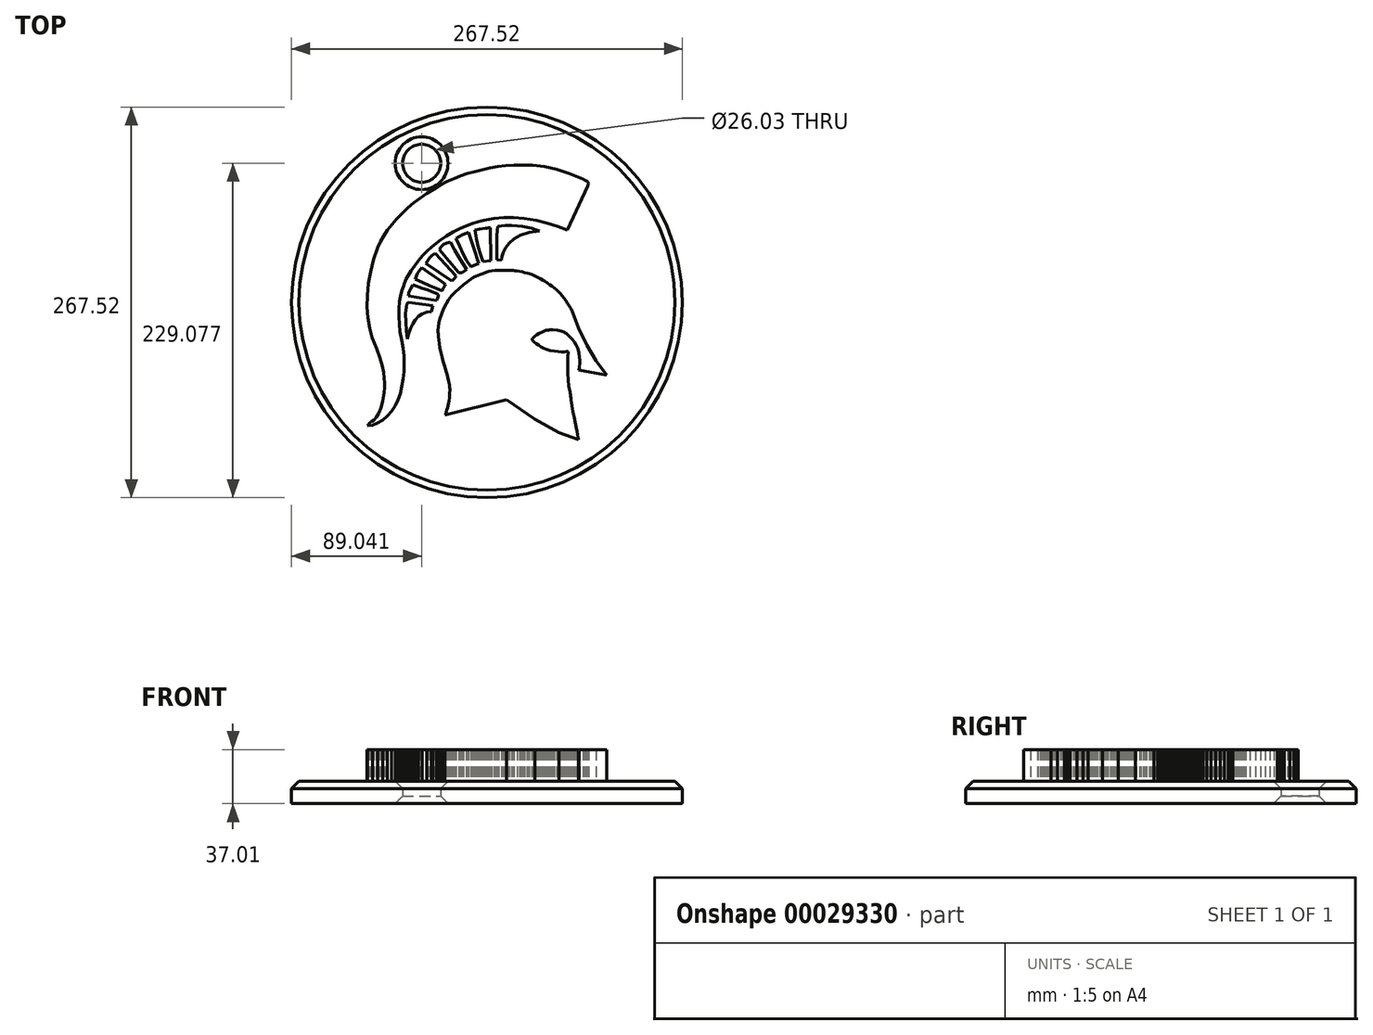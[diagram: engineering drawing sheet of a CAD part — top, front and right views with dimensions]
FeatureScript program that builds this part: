
annotation { "Feature Type Name" : "Feature", "Feature Type Description" : "" }
export const myFeature = defineFeature(function(context is Context, id is Id, definition is map)
    precondition{}
    {
        {
            var Q0;
            Q0=qCreatedBy(makeId("Top.planeOp"),FACE);
            var sketch = newSketch(context, id + "F0", { "sketchPlane" : qUnion([Q0])});
            skLineSegment(sketch, "E0", {"start": v(-81.82, -84.47) * mm, "end": v(-80.11, -82.47) * mm});
            skLineSegment(sketch, "E1", {"start": v(-80.11, -82.47) * mm, "end": v(-79.76, -82.32) * mm});
            skLineSegment(sketch, "E2", {"start": v(-79.76, -82.32) * mm, "end": v(-78.83, -81.76) * mm});
            skLineSegment(sketch, "E3", {"start": v(-78.83, -81.76) * mm, "end": v(-77.48, -80.64) * mm});
            skLineSegment(sketch, "E4", {"start": v(-77.48, -80.64) * mm, "end": v(-75.88, -78.83) * mm});
            skLineSegment(sketch, "E5", {"start": v(-75.88, -78.83) * mm, "end": v(-74.2, -76.16) * mm});
            skLineSegment(sketch, "E6", {"start": v(-74.2, -76.16) * mm, "end": v(-72.61, -72.5) * mm});
            skLineSegment(sketch, "E7", {"start": v(-72.61, -72.5) * mm, "end": v(-71.28, -67.7) * mm});
            skLineSegment(sketch, "E8", {"start": v(-71.28, -67.7) * mm, "end": v(-70.36, -61.6) * mm});
            skLineSegment(sketch, "E9", {"start": v(-70.36, -61.6) * mm, "end": v(-70.11, -58.43) * mm});
            skLineSegment(sketch, "E10", {"start": v(-70.11, -58.43) * mm, "end": v(-70.03, -55.21) * mm});
            skLineSegment(sketch, "E11", {"start": v(-70.03, -55.21) * mm, "end": v(-70.22, -51.75) * mm});
            skLineSegment(sketch, "E12", {"start": v(-70.22, -51.75) * mm, "end": v(-70.77, -47.86) * mm});
            skLineSegment(sketch, "E13", {"start": v(-70.77, -47.86) * mm, "end": v(-71.78, -43.35) * mm});
            skLineSegment(sketch, "E14", {"start": v(-71.78, -43.35) * mm, "end": v(-73.35, -38.02) * mm});
            skLineSegment(sketch, "E15", {"start": v(-73.35, -38.02) * mm, "end": v(-75.57, -31.7) * mm});
            skLineSegment(sketch, "E16", {"start": v(-75.57, -31.7) * mm, "end": v(-78.54, -24.17) * mm});
            skLineSegment(sketch, "E17", {"start": v(-78.54, -24.17) * mm, "end": v(-80.35, -17.68) * mm});
            skLineSegment(sketch, "E18", {"start": v(-80.35, -17.68) * mm, "end": v(-81.52, -10.62) * mm});
            skLineSegment(sketch, "E19", {"start": v(-81.52, -10.62) * mm, "end": v(-82.04, -3.1) * mm});
            skLineSegment(sketch, "E20", {"start": v(-82.04, -3.1) * mm, "end": v(-81.9, 4.77) * mm});
            skLineSegment(sketch, "E21", {"start": v(-81.9, 4.77) * mm, "end": v(-81.12, 12.88) * mm});
            skLineSegment(sketch, "E22", {"start": v(-81.12, 12.88) * mm, "end": v(-79.67, 21.1) * mm});
            skLineSegment(sketch, "E23", {"start": v(-79.67, 21.1) * mm, "end": v(-77.55, 29.32) * mm});
            skLineSegment(sketch, "E24", {"start": v(-77.55, 29.32) * mm, "end": v(-74.76, 37.44) * mm});
            skLineSegment(sketch, "E25", {"start": v(-74.76, 37.44) * mm, "end": v(-72.96, 41.45) * mm});
            skLineSegment(sketch, "E26", {"start": v(-72.96, 41.45) * mm, "end": v(-70.71, 45.46) * mm});
            skLineSegment(sketch, "E27", {"start": v(-70.71, 45.46) * mm, "end": v(-68.05, 49.45) * mm});
            skLineSegment(sketch, "E28", {"start": v(-68.05, 49.45) * mm, "end": v(-65.02, 53.39) * mm});
            skLineSegment(sketch, "E29", {"start": v(-65.02, 53.39) * mm, "end": v(-61.65, 57.26) * mm});
            skLineSegment(sketch, "E30", {"start": v(-61.65, 57.26) * mm, "end": v(-57.99, 61.03) * mm});
            skLineSegment(sketch, "E31", {"start": v(-57.99, 61.03) * mm, "end": v(-54.06, 64.68) * mm});
            skLineSegment(sketch, "E32", {"start": v(-54.06, 64.68) * mm, "end": v(-49.92, 68.19) * mm});
            skLineSegment(sketch, "E33", {"start": v(-49.92, 68.19) * mm, "end": v(-45.6, 71.53) * mm});
            skLineSegment(sketch, "E34", {"start": v(-45.6, 71.53) * mm, "end": v(-41.12, 74.68) * mm});
            skLineSegment(sketch, "E35", {"start": v(-41.12, 74.68) * mm, "end": v(-36.55, 77.6) * mm});
            skLineSegment(sketch, "E36", {"start": v(-36.55, 77.6) * mm, "end": v(-31.9, 80.3) * mm});
            skLineSegment(sketch, "E37", {"start": v(-31.9, 80.3) * mm, "end": v(-27.23, 82.72) * mm});
            skLineSegment(sketch, "E38", {"start": v(-27.23, 82.72) * mm, "end": v(-22.57, 84.86) * mm});
            skLineSegment(sketch, "E39", {"start": v(-22.57, 84.86) * mm, "end": v(-17.96, 86.68) * mm});
            skLineSegment(sketch, "E40", {"start": v(-17.96, 86.68) * mm, "end": v(-13.43, 88.16) * mm});
            skLineSegment(sketch, "E41", {"start": v(-13.43, 88.16) * mm, "end": v(-8.18, 89.63) * mm});
            skLineSegment(sketch, "E42", {"start": v(-8.18, 89.63) * mm, "end": v(-3.03, 90.91) * mm});
            skLineSegment(sketch, "E43", {"start": v(-3.03, 90.91) * mm, "end": v(2.11, 92) * mm});
            skLineSegment(sketch, "E44", {"start": v(2.11, 92) * mm, "end": v(7.35, 92.87) * mm});
            skLineSegment(sketch, "E45", {"start": v(7.35, 92.87) * mm, "end": v(12.8, 93.51) * mm});
            skLineSegment(sketch, "E46", {"start": v(12.8, 93.51) * mm, "end": v(18.53, 93.92) * mm});
            skLineSegment(sketch, "E47", {"start": v(18.53, 93.92) * mm, "end": v(24.67, 94.08) * mm});
            skLineSegment(sketch, "E48", {"start": v(24.67, 94.08) * mm, "end": v(31.31, 93.97) * mm});
            skLineSegment(sketch, "E49", {"start": v(31.31, 93.97) * mm, "end": v(39.54, 93.1) * mm});
            skLineSegment(sketch, "E50", {"start": v(39.54, 93.1) * mm, "end": v(47.72, 91.15) * mm});
            skLineSegment(sketch, "E51", {"start": v(47.72, 91.15) * mm, "end": v(56.34, 88.2) * mm});
            skLineSegment(sketch, "E52", {"start": v(56.34, 88.2) * mm, "end": v(65.9, 84.32) * mm});
            skLineSegment(sketch, "E53", {"start": v(65.9, 84.32) * mm, "end": v(66.02, 84.26) * mm});
            skLineSegment(sketch, "E54", {"start": v(66.02, 84.26) * mm, "end": v(66.35, 84.09) * mm});
            skLineSegment(sketch, "E55", {"start": v(66.35, 84.09) * mm, "end": v(66.82, 83.84) * mm});
            skLineSegment(sketch, "E56", {"start": v(66.82, 83.84) * mm, "end": v(67.38, 83.52) * mm});
            skLineSegment(sketch, "E57", {"start": v(67.38, 83.52) * mm, "end": v(67.97, 83.16) * mm});
            skLineSegment(sketch, "E58", {"start": v(67.97, 83.16) * mm, "end": v(68.54, 82.77) * mm});
            skLineSegment(sketch, "E59", {"start": v(68.54, 82.77) * mm, "end": v(69.01, 82.39) * mm});
            skLineSegment(sketch, "E60", {"start": v(69.01, 82.39) * mm, "end": v(69.34, 82.02) * mm});
            skLineSegment(sketch, "E61", {"start": v(69.34, 82.02) * mm, "end": v(69.55, 81.28) * mm});
            skLineSegment(sketch, "E62", {"start": v(69.55, 81.28) * mm, "end": v(69.37, 80.54) * mm});
            skLineSegment(sketch, "E63", {"start": v(69.37, 80.54) * mm, "end": v(69.07, 79.97) * mm});
            skLineSegment(sketch, "E64", {"start": v(69.07, 79.97) * mm, "end": v(68.92, 79.74) * mm});
            skLineSegment(sketch, "E65", {"start": v(68.92, 79.74) * mm, "end": v(55.1, 49.38) * mm});
            skLineSegment(sketch, "E66", {"start": v(55.1, 49.38) * mm, "end": v(48.24, 52.04) * mm});
            skLineSegment(sketch, "E67", {"start": v(48.24, 52.04) * mm, "end": v(41.22, 54.4) * mm});
            skLineSegment(sketch, "E68", {"start": v(41.22, 54.4) * mm, "end": v(33.72, 56.27) * mm});
            skLineSegment(sketch, "E69", {"start": v(33.72, 56.27) * mm, "end": v(25.43, 57.47) * mm});
            skLineSegment(sketch, "E70", {"start": v(25.43, 57.47) * mm, "end": v(18.16, 57.96) * mm});
            skLineSegment(sketch, "E71", {"start": v(18.16, 57.96) * mm, "end": v(11.43, 57.98) * mm});
            skLineSegment(sketch, "E72", {"start": v(11.43, 57.98) * mm, "end": v(4.83, 57.42) * mm});
            skLineSegment(sketch, "E73", {"start": v(4.83, 57.42) * mm, "end": v(-2.08, 56.17) * mm});
            skLineSegment(sketch, "E74", {"start": v(-2.08, 56.17) * mm, "end": v(-5.93, 55.2) * mm});
            skLineSegment(sketch, "E75", {"start": v(-5.93, 55.2) * mm, "end": v(-9.96, 53.98) * mm});
            skLineSegment(sketch, "E76", {"start": v(-9.96, 53.98) * mm, "end": v(-14.18, 52.43) * mm});
            skLineSegment(sketch, "E77", {"start": v(-14.18, 52.43) * mm, "end": v(-18.58, 50.5) * mm});
            skLineSegment(sketch, "E78", {"start": v(-18.58, 50.5) * mm, "end": v(-23.16, 48.14) * mm});
            skLineSegment(sketch, "E79", {"start": v(-23.16, 48.14) * mm, "end": v(-27.92, 45.3) * mm});
            skLineSegment(sketch, "E80", {"start": v(-27.92, 45.3) * mm, "end": v(-32.85, 41.88) * mm});
            skLineSegment(sketch, "E81", {"start": v(-32.85, 41.88) * mm, "end": v(-37.97, 37.87) * mm});
            skLineSegment(sketch, "E82", {"start": v(-37.97, 37.87) * mm, "end": v(-40.92, 35.16) * mm});
            skLineSegment(sketch, "E83", {"start": v(-40.92, 35.16) * mm, "end": v(-43.9, 32) * mm});
            skLineSegment(sketch, "E84", {"start": v(-43.9, 32) * mm, "end": v(-46.82, 28.56) * mm});
            skLineSegment(sketch, "E85", {"start": v(-46.82, 28.56) * mm, "end": v(-49.52, 25.05) * mm});
            skLineSegment(sketch, "E86", {"start": v(-49.52, 25.05) * mm, "end": v(-51.92, 21.65) * mm});
            skLineSegment(sketch, "E87", {"start": v(-51.92, 21.65) * mm, "end": v(-53.9, 18.55) * mm});
            skLineSegment(sketch, "E88", {"start": v(-53.9, 18.55) * mm, "end": v(-55.32, 15.94) * mm});
            skLineSegment(sketch, "E89", {"start": v(-55.32, 15.94) * mm, "end": v(-56.1, 14) * mm});
            skLineSegment(sketch, "E90", {"start": v(-56.1, 14) * mm, "end": v(-56.4, 13.21) * mm});
            skLineSegment(sketch, "E91", {"start": v(-56.4, 13.21) * mm, "end": v(-57.17, 11.04) * mm});
            skLineSegment(sketch, "E92", {"start": v(-57.17, 11.04) * mm, "end": v(-58.17, 7.82) * mm});
            skLineSegment(sketch, "E93", {"start": v(-58.17, 7.82) * mm, "end": v(-59.22, 3.9) * mm});
            skLineSegment(sketch, "E94", {"start": v(-59.22, 3.9) * mm, "end": v(-59.9, 0.65) * mm});
            skLineSegment(sketch, "E95", {"start": v(-59.9, 0.65) * mm, "end": v(-60.33, -4.33) * mm});
            skLineSegment(sketch, "E96", {"start": v(-60.33, -4.33) * mm, "end": v(-60.2, -9.72) * mm});
            skLineSegment(sketch, "E97", {"start": v(-60.2, -9.72) * mm, "end": v(-59.8, -15.07) * mm});
            skLineSegment(sketch, "E98", {"start": v(-59.8, -15.07) * mm, "end": v(-59.47, -19.88) * mm});
            skLineSegment(sketch, "E99", {"start": v(-59.47, -19.88) * mm, "end": v(-58.37, -26.08) * mm});
            skLineSegment(sketch, "E100", {"start": v(-58.37, -26.08) * mm, "end": v(-57.47, -31.55) * mm});
            skLineSegment(sketch, "E101", {"start": v(-57.47, -31.55) * mm, "end": v(-56.84, -36.7) * mm});
            skLineSegment(sketch, "E102", {"start": v(-56.84, -36.7) * mm, "end": v(-56.58, -41.88) * mm});
            skLineSegment(sketch, "E103", {"start": v(-56.58, -41.88) * mm, "end": v(-56.78, -47.2) * mm});
            skLineSegment(sketch, "E104", {"start": v(-56.78, -47.2) * mm, "end": v(-57.38, -52.46) * mm});
            skLineSegment(sketch, "E105", {"start": v(-57.38, -52.46) * mm, "end": v(-58.28, -57.61) * mm});
            skLineSegment(sketch, "E106", {"start": v(-58.28, -57.61) * mm, "end": v(-59.36, -62.55) * mm});
            skLineSegment(sketch, "E107", {"start": v(-59.36, -62.55) * mm, "end": v(-60.7, -66.75) * mm});
            skLineSegment(sketch, "E108", {"start": v(-60.7, -66.75) * mm, "end": v(-62.66, -70.77) * mm});
            skLineSegment(sketch, "E109", {"start": v(-62.66, -70.77) * mm, "end": v(-65.13, -74.48) * mm});
            skLineSegment(sketch, "E110", {"start": v(-65.13, -74.48) * mm, "end": v(-68.03, -77.78) * mm});
            skLineSegment(sketch, "E111", {"start": v(-68.03, -77.78) * mm, "end": v(-71.24, -80.55) * mm});
            skLineSegment(sketch, "E112", {"start": v(-71.24, -80.55) * mm, "end": v(-74.68, -82.66) * mm});
            skLineSegment(sketch, "E113", {"start": v(-74.68, -82.66) * mm, "end": v(-78.24, -84) * mm});
            skLineSegment(sketch, "E114", {"start": v(-78.24, -84) * mm, "end": v(-81.82, -84.47) * mm});
            skLineSegment(sketch, "E115", {"start": v(-54.53, -25.24) * mm, "end": v(-55.07, -19.51) * mm});
            skLineSegment(sketch, "E116", {"start": v(-55.07, -19.51) * mm, "end": v(-55.59, -13.77) * mm});
            skLineSegment(sketch, "E117", {"start": v(-55.59, -13.77) * mm, "end": v(-55.65, -7.67) * mm});
            skLineSegment(sketch, "E118", {"start": v(-55.65, -7.67) * mm, "end": v(-54.81, -0.87) * mm});
            skLineSegment(sketch, "E119", {"start": v(-54.81, -0.87) * mm, "end": v(-53.88, 0.13) * mm});
            skLineSegment(sketch, "E120", {"start": v(-53.88, 0.13) * mm, "end": v(-37.13, -2.22) * mm});
            skLineSegment(sketch, "E121", {"start": v(-37.13, -2.22) * mm, "end": v(-37.85, -6.21) * mm});
            skLineSegment(sketch, "E122", {"start": v(-37.85, -6.21) * mm, "end": v(-41.3, -6.74) * mm});
            skLineSegment(sketch, "E123", {"start": v(-41.3, -6.74) * mm, "end": v(-44.26, -7.92) * mm});
            skLineSegment(sketch, "E124", {"start": v(-44.26, -7.92) * mm, "end": v(-46.8, -9.68) * mm});
            skLineSegment(sketch, "E125", {"start": v(-46.8, -9.68) * mm, "end": v(-48.95, -11.97) * mm});
            skLineSegment(sketch, "E126", {"start": v(-48.95, -11.97) * mm, "end": v(-50.75, -14.73) * mm});
            skLineSegment(sketch, "E127", {"start": v(-50.75, -14.73) * mm, "end": v(-52.26, -17.9) * mm});
            skLineSegment(sketch, "E128", {"start": v(-52.26, -17.9) * mm, "end": v(-53.5, -21.42) * mm});
            skLineSegment(sketch, "E129", {"start": v(-53.5, -21.42) * mm, "end": v(-54.53, -25.24) * mm});
            skLineSegment(sketch, "E130", {"start": v(-28.63, -77.13) * mm, "end": v(-28.54, -76.85) * mm});
            skLineSegment(sketch, "E131", {"start": v(-28.54, -76.85) * mm, "end": v(-28.29, -76.07) * mm});
            skLineSegment(sketch, "E132", {"start": v(-28.29, -76.07) * mm, "end": v(-27.92, -74.93) * mm});
            skLineSegment(sketch, "E133", {"start": v(-27.92, -74.93) * mm, "end": v(-27.48, -73.52) * mm});
            skLineSegment(sketch, "E134", {"start": v(-27.48, -73.52) * mm, "end": v(-27.02, -71.97) * mm});
            skLineSegment(sketch, "E135", {"start": v(-27.02, -71.97) * mm, "end": v(-26.57, -70.4) * mm});
            skLineSegment(sketch, "E136", {"start": v(-26.57, -70.4) * mm, "end": v(-26.18, -68.9) * mm});
            skLineSegment(sketch, "E137", {"start": v(-26.18, -68.9) * mm, "end": v(-25.9, -67.6) * mm});
            skLineSegment(sketch, "E138", {"start": v(-25.9, -67.6) * mm, "end": v(-25.58, -64.97) * mm});
            skLineSegment(sketch, "E139", {"start": v(-25.58, -64.97) * mm, "end": v(-25.44, -62.18) * mm});
            skLineSegment(sketch, "E140", {"start": v(-25.44, -62.18) * mm, "end": v(-25.4, -59.98) * mm});
            skLineSegment(sketch, "E141", {"start": v(-25.4, -59.98) * mm, "end": v(-25.4, -59.09) * mm});
            skLineSegment(sketch, "E142", {"start": v(-25.4, -59.09) * mm, "end": v(-25.5, -58.38) * mm});
            skLineSegment(sketch, "E143", {"start": v(-25.5, -58.38) * mm, "end": v(-25.75, -56.56) * mm});
            skLineSegment(sketch, "E144", {"start": v(-25.75, -56.56) * mm, "end": v(-26.19, -54.03) * mm});
            skLineSegment(sketch, "E145", {"start": v(-26.19, -54.03) * mm, "end": v(-26.82, -51.22) * mm});
            skLineSegment(sketch, "E146", {"start": v(-26.82, -51.22) * mm, "end": v(-27.25, -49.6) * mm});
            skLineSegment(sketch, "E147", {"start": v(-27.25, -49.6) * mm, "end": v(-27.8, -47.67) * mm});
            skLineSegment(sketch, "E148", {"start": v(-27.8, -47.67) * mm, "end": v(-28.42, -45.53) * mm});
            skLineSegment(sketch, "E149", {"start": v(-28.42, -45.53) * mm, "end": v(-29.06, -43.3) * mm});
            skLineSegment(sketch, "E150", {"start": v(-29.06, -43.3) * mm, "end": v(-29.69, -41.13) * mm});
            skLineSegment(sketch, "E151", {"start": v(-29.69, -41.13) * mm, "end": v(-30.25, -39.11) * mm});
            skLineSegment(sketch, "E152", {"start": v(-30.25, -39.11) * mm, "end": v(-30.71, -37.4) * mm});
            skLineSegment(sketch, "E153", {"start": v(-30.71, -37.4) * mm, "end": v(-31.02, -36.08) * mm});
            skLineSegment(sketch, "E154", {"start": v(-31.02, -36.08) * mm, "end": v(-31.67, -33.63) * mm});
            skLineSegment(sketch, "E155", {"start": v(-31.67, -33.63) * mm, "end": v(-32.2, -30.97) * mm});
            skLineSegment(sketch, "E156", {"start": v(-32.2, -30.97) * mm, "end": v(-32.63, -28.27) * mm});
            skLineSegment(sketch, "E157", {"start": v(-32.63, -28.27) * mm, "end": v(-32.95, -25.69) * mm});
            skLineSegment(sketch, "E158", {"start": v(-32.95, -25.69) * mm, "end": v(-33.2, -23.4) * mm});
            skLineSegment(sketch, "E159", {"start": v(-33.2, -23.4) * mm, "end": v(-33.35, -21.55) * mm});
            skLineSegment(sketch, "E160", {"start": v(-33.35, -21.55) * mm, "end": v(-33.44, -20.32) * mm});
            skLineSegment(sketch, "E161", {"start": v(-33.44, -20.32) * mm, "end": v(-33.47, -19.88) * mm});
            skLineSegment(sketch, "E162", {"start": v(-33.47, -19.88) * mm, "end": v(-33.4, -18.95) * mm});
            skLineSegment(sketch, "E163", {"start": v(-33.4, -18.95) * mm, "end": v(-33.16, -16.7) * mm});
            skLineSegment(sketch, "E164", {"start": v(-33.16, -16.7) * mm, "end": v(-32.78, -13.95) * mm});
            skLineSegment(sketch, "E165", {"start": v(-32.78, -13.95) * mm, "end": v(-32.25, -11.5) * mm});
            skLineSegment(sketch, "E166", {"start": v(-32.25, -11.5) * mm, "end": v(-31.06, -7.95) * mm});
            skLineSegment(sketch, "E167", {"start": v(-31.06, -7.95) * mm, "end": v(-29.6, -4.42) * mm});
            skLineSegment(sketch, "E168", {"start": v(-29.6, -4.42) * mm, "end": v(-27.95, -1.1) * mm});
            skLineSegment(sketch, "E169", {"start": v(-27.95, -1.1) * mm, "end": v(-26.22, 1.82) * mm});
            skLineSegment(sketch, "E170", {"start": v(-26.22, 1.82) * mm, "end": v(-24.28, 4.32) * mm});
            skLineSegment(sketch, "E171", {"start": v(-24.28, 4.32) * mm, "end": v(-21.77, 6.93) * mm});
            skLineSegment(sketch, "E172", {"start": v(-21.77, 6.93) * mm, "end": v(-18.95, 9.51) * mm});
            skLineSegment(sketch, "E173", {"start": v(-18.95, 9.51) * mm, "end": v(-16.07, 11.92) * mm});
            skLineSegment(sketch, "E174", {"start": v(-16.07, 11.92) * mm, "end": v(-13.4, 14.04) * mm});
            skLineSegment(sketch, "E175", {"start": v(-13.4, 14.04) * mm, "end": v(-11.17, 15.71) * mm});
            skLineSegment(sketch, "E176", {"start": v(-11.17, 15.71) * mm, "end": v(-9.64, 16.82) * mm});
            skLineSegment(sketch, "E177", {"start": v(-9.64, 16.82) * mm, "end": v(-9.08, 17.21) * mm});
            skLineSegment(sketch, "E178", {"start": v(-9.08, 17.21) * mm, "end": v(-8.73, 17.37) * mm});
            skLineSegment(sketch, "E179", {"start": v(-8.73, 17.37) * mm, "end": v(-7.79, 17.78) * mm});
            skLineSegment(sketch, "E180", {"start": v(-7.79, 17.78) * mm, "end": v(-6.36, 18.37) * mm});
            skLineSegment(sketch, "E181", {"start": v(-6.36, 18.37) * mm, "end": v(-4.6, 19.08) * mm});
            skLineSegment(sketch, "E182", {"start": v(-4.6, 19.08) * mm, "end": v(-2.63, 19.82) * mm});
            skLineSegment(sketch, "E183", {"start": v(-2.63, 19.82) * mm, "end": v(-0.57, 20.54) * mm});
            skLineSegment(sketch, "E184", {"start": v(-0.57, 20.54) * mm, "end": v(1.43, 21.14) * mm});
            skLineSegment(sketch, "E185", {"start": v(1.43, 21.14) * mm, "end": v(3.26, 21.57) * mm});
            skLineSegment(sketch, "E186", {"start": v(3.26, 21.57) * mm, "end": v(5.53, 21.8) * mm});
            skLineSegment(sketch, "E187", {"start": v(5.53, 21.8) * mm, "end": v(7.95, 21.93) * mm});
            skLineSegment(sketch, "E188", {"start": v(7.95, 21.93) * mm, "end": v(10.39, 22) * mm});
            skLineSegment(sketch, "E189", {"start": v(10.39, 22) * mm, "end": v(12.7, 22.02) * mm});
            skLineSegment(sketch, "E190", {"start": v(12.7, 22.02) * mm, "end": v(14.74, 22) * mm});
            skLineSegment(sketch, "E191", {"start": v(14.74, 22) * mm, "end": v(16.37, 21.98) * mm});
            skLineSegment(sketch, "E192", {"start": v(16.37, 21.98) * mm, "end": v(17.45, 21.96) * mm});
            skLineSegment(sketch, "E193", {"start": v(17.45, 21.96) * mm, "end": v(17.84, 21.95) * mm});
            skLineSegment(sketch, "E194", {"start": v(17.84, 21.95) * mm, "end": v(18.18, 21.9) * mm});
            skLineSegment(sketch, "E195", {"start": v(18.18, 21.9) * mm, "end": v(19.13, 21.74) * mm});
            skLineSegment(sketch, "E196", {"start": v(19.13, 21.74) * mm, "end": v(20.53, 21.5) * mm});
            skLineSegment(sketch, "E197", {"start": v(20.53, 21.5) * mm, "end": v(22.23, 21.19) * mm});
            skLineSegment(sketch, "E198", {"start": v(22.23, 21.19) * mm, "end": v(24.1, 20.82) * mm});
            skLineSegment(sketch, "E199", {"start": v(24.1, 20.82) * mm, "end": v(25.96, 20.43) * mm});
            skLineSegment(sketch, "E200", {"start": v(25.96, 20.43) * mm, "end": v(27.69, 20.01) * mm});
            skLineSegment(sketch, "E201", {"start": v(27.69, 20.01) * mm, "end": v(29.13, 19.6) * mm});
            skLineSegment(sketch, "E202", {"start": v(29.13, 19.6) * mm, "end": v(30.92, 18.92) * mm});
            skLineSegment(sketch, "E203", {"start": v(30.92, 18.92) * mm, "end": v(32.84, 18.06) * mm});
            skLineSegment(sketch, "E204", {"start": v(32.84, 18.06) * mm, "end": v(34.77, 17.1) * mm});
            skLineSegment(sketch, "E205", {"start": v(34.77, 17.1) * mm, "end": v(36.61, 16.13) * mm});
            skLineSegment(sketch, "E206", {"start": v(36.61, 16.13) * mm, "end": v(38.24, 15.23) * mm});
            skLineSegment(sketch, "E207", {"start": v(38.24, 15.23) * mm, "end": v(39.54, 14.48) * mm});
            skLineSegment(sketch, "E208", {"start": v(39.54, 14.48) * mm, "end": v(40.4, 13.97) * mm});
            skLineSegment(sketch, "E209", {"start": v(40.4, 13.97) * mm, "end": v(40.71, 13.79) * mm});
            skLineSegment(sketch, "E210", {"start": v(40.71, 13.79) * mm, "end": v(41.01, 13.57) * mm});
            skLineSegment(sketch, "E211", {"start": v(41.01, 13.57) * mm, "end": v(41.82, 12.99) * mm});
            skLineSegment(sketch, "E212", {"start": v(41.82, 12.99) * mm, "end": v(43, 12.1) * mm});
            skLineSegment(sketch, "E213", {"start": v(43, 12.1) * mm, "end": v(44.45, 11) * mm});
            skLineSegment(sketch, "E214", {"start": v(44.45, 11) * mm, "end": v(46.03, 9.75) * mm});
            skLineSegment(sketch, "E215", {"start": v(46.03, 9.75) * mm, "end": v(47.62, 8.44) * mm});
            skLineSegment(sketch, "E216", {"start": v(47.62, 8.44) * mm, "end": v(49.08, 7.15) * mm});
            skLineSegment(sketch, "E217", {"start": v(49.08, 7.15) * mm, "end": v(50.3, 5.94) * mm});
            skLineSegment(sketch, "E218", {"start": v(50.3, 5.94) * mm, "end": v(51.48, 4.57) * mm});
            skLineSegment(sketch, "E219", {"start": v(51.48, 4.57) * mm, "end": v(52.74, 2.92) * mm});
            skLineSegment(sketch, "E220", {"start": v(52.74, 2.92) * mm, "end": v(54, 1.15) * mm});
            skLineSegment(sketch, "E221", {"start": v(54, 1.15) * mm, "end": v(55.2, -0.6) * mm});
            skLineSegment(sketch, "E222", {"start": v(55.2, -0.6) * mm, "end": v(56.24, -2.21) * mm});
            skLineSegment(sketch, "E223", {"start": v(56.24, -2.21) * mm, "end": v(57.09, -3.54) * mm});
            skLineSegment(sketch, "E224", {"start": v(57.09, -3.54) * mm, "end": v(57.65, -4.43) * mm});
            skLineSegment(sketch, "E225", {"start": v(57.65, -4.43) * mm, "end": v(57.85, -4.76) * mm});
            skLineSegment(sketch, "E226", {"start": v(57.85, -4.76) * mm, "end": v(62.78, -17.36) * mm});
            skLineSegment(sketch, "E227", {"start": v(62.78, -17.36) * mm, "end": v(68.43, -29.1) * mm});
            skLineSegment(sketch, "E228", {"start": v(68.43, -29.1) * mm, "end": v(74.84, -39.93) * mm});
            skLineSegment(sketch, "E229", {"start": v(74.84, -39.93) * mm, "end": v(82.04, -49.81) * mm});
            skLineSegment(sketch, "E230", {"start": v(82.04, -49.81) * mm, "end": v(62.89, -46.29) * mm});
            skLineSegment(sketch, "E231", {"start": v(62.89, -46.29) * mm, "end": v(62.97, -45.98) * mm});
            skLineSegment(sketch, "E232", {"start": v(62.97, -45.98) * mm, "end": v(63.16, -45.1) * mm});
            skLineSegment(sketch, "E233", {"start": v(63.16, -45.1) * mm, "end": v(63.38, -43.74) * mm});
            skLineSegment(sketch, "E234", {"start": v(63.38, -43.74) * mm, "end": v(63.55, -41.94) * mm});
            skLineSegment(sketch, "E235", {"start": v(63.55, -41.94) * mm, "end": v(63.6, -39.79) * mm});
            skLineSegment(sketch, "E236", {"start": v(63.6, -39.79) * mm, "end": v(63.43, -37.34) * mm});
            skLineSegment(sketch, "E237", {"start": v(63.43, -37.34) * mm, "end": v(63, -34.68) * mm});
            skLineSegment(sketch, "E238", {"start": v(63, -34.68) * mm, "end": v(62.2, -31.86) * mm});
            skLineSegment(sketch, "E239", {"start": v(62.2, -31.86) * mm, "end": v(61.05, -29.23) * mm});
            skLineSegment(sketch, "E240", {"start": v(61.05, -29.23) * mm, "end": v(59.7, -26.95) * mm});
            skLineSegment(sketch, "E241", {"start": v(59.7, -26.95) * mm, "end": v(58.23, -25.03) * mm});
            skLineSegment(sketch, "E242", {"start": v(58.23, -25.03) * mm, "end": v(56.77, -23.46) * mm});
            skLineSegment(sketch, "E243", {"start": v(56.77, -23.46) * mm, "end": v(55.43, -22.24) * mm});
            skLineSegment(sketch, "E244", {"start": v(55.43, -22.24) * mm, "end": v(54.33, -21.38) * mm});
            skLineSegment(sketch, "E245", {"start": v(54.33, -21.38) * mm, "end": v(53.59, -20.86) * mm});
            skLineSegment(sketch, "E246", {"start": v(53.59, -20.86) * mm, "end": v(53.31, -20.69) * mm});
            skLineSegment(sketch, "E247", {"start": v(53.31, -20.69) * mm, "end": v(52.71, -20.39) * mm});
            skLineSegment(sketch, "E248", {"start": v(52.71, -20.39) * mm, "end": v(51.03, -19.73) * mm});
            skLineSegment(sketch, "E249", {"start": v(51.03, -19.73) * mm, "end": v(48.48, -19.05) * mm});
            skLineSegment(sketch, "E250", {"start": v(48.48, -19.05) * mm, "end": v(45.26, -18.71) * mm});
            skLineSegment(sketch, "E251", {"start": v(45.26, -18.71) * mm, "end": v(44.61, -18.72) * mm});
            skLineSegment(sketch, "E252", {"start": v(44.61, -18.72) * mm, "end": v(43.86, -18.77) * mm});
            skLineSegment(sketch, "E253", {"start": v(43.86, -18.77) * mm, "end": v(43.05, -18.83) * mm});
            skLineSegment(sketch, "E254", {"start": v(43.05, -18.83) * mm, "end": v(42.25, -18.91) * mm});
            skLineSegment(sketch, "E255", {"start": v(42.25, -18.91) * mm, "end": v(41.52, -18.99) * mm});
            skLineSegment(sketch, "E256", {"start": v(41.52, -18.99) * mm, "end": v(40.92, -19.06) * mm});
            skLineSegment(sketch, "E257", {"start": v(40.92, -19.06) * mm, "end": v(40.51, -19.1) * mm});
            skLineSegment(sketch, "E258", {"start": v(40.51, -19.1) * mm, "end": v(40.37, -19.13) * mm});
            skLineSegment(sketch, "E259", {"start": v(40.37, -19.13) * mm, "end": v(37.89, -20.17) * mm});
            skLineSegment(sketch, "E260", {"start": v(37.89, -20.17) * mm, "end": v(35.84, -21.26) * mm});
            skLineSegment(sketch, "E261", {"start": v(35.84, -21.26) * mm, "end": v(34.18, -22.33) * mm});
            skLineSegment(sketch, "E262", {"start": v(34.18, -22.33) * mm, "end": v(32.9, -23.33) * mm});
            skLineSegment(sketch, "E263", {"start": v(32.9, -23.33) * mm, "end": v(31.94, -24.2) * mm});
            skLineSegment(sketch, "E264", {"start": v(31.94, -24.2) * mm, "end": v(31.3, -24.9) * mm});
            skLineSegment(sketch, "E265", {"start": v(31.3, -24.9) * mm, "end": v(30.94, -25.36) * mm});
            skLineSegment(sketch, "E266", {"start": v(30.94, -25.36) * mm, "end": v(30.82, -25.52) * mm});
            skLineSegment(sketch, "E267", {"start": v(30.82, -25.52) * mm, "end": v(31.05, -25.74) * mm});
            skLineSegment(sketch, "E268", {"start": v(31.05, -25.74) * mm, "end": v(31.67, -26.32) * mm});
            skLineSegment(sketch, "E269", {"start": v(31.67, -26.32) * mm, "end": v(32.64, -27.17) * mm});
            skLineSegment(sketch, "E270", {"start": v(32.64, -27.17) * mm, "end": v(33.9, -28.2) * mm});
            skLineSegment(sketch, "E271", {"start": v(33.9, -28.2) * mm, "end": v(35.38, -29.3) * mm});
            skLineSegment(sketch, "E272", {"start": v(35.38, -29.3) * mm, "end": v(37.03, -30.37) * mm});
            skLineSegment(sketch, "E273", {"start": v(37.03, -30.37) * mm, "end": v(38.79, -31.33) * mm});
            skLineSegment(sketch, "E274", {"start": v(38.79, -31.33) * mm, "end": v(40.6, -32.08) * mm});
            skLineSegment(sketch, "E275", {"start": v(40.6, -32.08) * mm, "end": v(43.43, -32.87) * mm});
            skLineSegment(sketch, "E276", {"start": v(43.43, -32.87) * mm, "end": v(46.16, -33.4) * mm});
            skLineSegment(sketch, "E277", {"start": v(46.16, -33.4) * mm, "end": v(48.7, -33.7) * mm});
            skLineSegment(sketch, "E278", {"start": v(48.7, -33.7) * mm, "end": v(50.97, -33.83) * mm});
            skLineSegment(sketch, "E279", {"start": v(50.97, -33.83) * mm, "end": v(52.88, -33.85) * mm});
            skLineSegment(sketch, "E280", {"start": v(52.88, -33.85) * mm, "end": v(54.35, -33.8) * mm});
            skLineSegment(sketch, "E281", {"start": v(54.35, -33.8) * mm, "end": v(55.3, -33.72) * mm});
            skLineSegment(sketch, "E282", {"start": v(55.3, -33.72) * mm, "end": v(55.63, -33.69) * mm});
            skLineSegment(sketch, "E283", {"start": v(55.63, -33.69) * mm, "end": v(55.59, -34.5) * mm});
            skLineSegment(sketch, "E284", {"start": v(55.59, -34.5) * mm, "end": v(55.48, -36.71) * mm});
            skLineSegment(sketch, "E285", {"start": v(55.48, -36.71) * mm, "end": v(55.38, -40.01) * mm});
            skLineSegment(sketch, "E286", {"start": v(55.38, -40.01) * mm, "end": v(55.34, -44.07) * mm});
            skLineSegment(sketch, "E287", {"start": v(55.34, -44.07) * mm, "end": v(55.41, -48.56) * mm});
            skLineSegment(sketch, "E288", {"start": v(55.41, -48.56) * mm, "end": v(55.65, -53.17) * mm});
            skLineSegment(sketch, "E289", {"start": v(55.65, -53.17) * mm, "end": v(56.13, -57.56) * mm});
            skLineSegment(sketch, "E290", {"start": v(56.13, -57.56) * mm, "end": v(56.89, -61.42) * mm});
            skLineSegment(sketch, "E291", {"start": v(56.89, -61.42) * mm, "end": v(57.04, -62.2) * mm});
            skLineSegment(sketch, "E292", {"start": v(57.04, -62.2) * mm, "end": v(57.14, -62.89) * mm});
            skLineSegment(sketch, "E293", {"start": v(57.14, -62.89) * mm, "end": v(57.32, -64.36) * mm});
            skLineSegment(sketch, "E294", {"start": v(57.32, -64.36) * mm, "end": v(57.42, -65.36) * mm});
            skLineSegment(sketch, "E295", {"start": v(57.42, -65.36) * mm, "end": v(57.48, -65.83) * mm});
            skLineSegment(sketch, "E296", {"start": v(57.48, -65.83) * mm, "end": v(57.53, -66.17) * mm});
            skLineSegment(sketch, "E297", {"start": v(57.53, -66.17) * mm, "end": v(57.6, -66.74) * mm});
            skLineSegment(sketch, "E298", {"start": v(57.6, -66.74) * mm, "end": v(58.17, -70.86) * mm});
            skLineSegment(sketch, "E299", {"start": v(58.17, -70.86) * mm, "end": v(58.97, -75.1) * mm});
            skLineSegment(sketch, "E300", {"start": v(58.97, -75.1) * mm, "end": v(59.76, -78.71) * mm});
            skLineSegment(sketch, "E301", {"start": v(59.76, -78.71) * mm, "end": v(60.48, -82.18) * mm});
            skLineSegment(sketch, "E302", {"start": v(60.48, -82.18) * mm, "end": v(61.12, -85.4) * mm});
            skLineSegment(sketch, "E303", {"start": v(61.12, -85.4) * mm, "end": v(61.68, -88.25) * mm});
            skLineSegment(sketch, "E304", {"start": v(61.68, -88.25) * mm, "end": v(62.13, -90.64) * mm});
            skLineSegment(sketch, "E305", {"start": v(62.13, -90.64) * mm, "end": v(62.47, -92.48) * mm});
            skLineSegment(sketch, "E306", {"start": v(62.47, -92.48) * mm, "end": v(62.68, -93.66) * mm});
            skLineSegment(sketch, "E307", {"start": v(62.68, -93.66) * mm, "end": v(62.76, -94.08) * mm});
            skLineSegment(sketch, "E308", {"start": v(62.76, -94.08) * mm, "end": v(49.18, -89.1) * mm});
            skLineSegment(sketch, "E309", {"start": v(49.18, -89.1) * mm, "end": v(32.97, -79.9) * mm});
            skLineSegment(sketch, "E310", {"start": v(32.97, -79.9) * mm, "end": v(13.4, -66.65) * mm});
            skLineSegment(sketch, "E311", {"start": v(13.4, -66.65) * mm, "end": v(-28.63, -77.13) * mm});
            skLineSegment(sketch, "E312", {"start": v(6.91, 29.14) * mm, "end": v(6.77, 34.65) * mm});
            skLineSegment(sketch, "E313", {"start": v(6.77, 34.65) * mm, "end": v(6.71, 40.24) * mm});
            skLineSegment(sketch, "E314", {"start": v(6.71, 40.24) * mm, "end": v(6.86, 46) * mm});
            skLineSegment(sketch, "E315", {"start": v(6.86, 46) * mm, "end": v(7.34, 52.02) * mm});
            skLineSegment(sketch, "E316", {"start": v(7.34, 52.02) * mm, "end": v(12.42, 52.54) * mm});
            skLineSegment(sketch, "E317", {"start": v(12.42, 52.54) * mm, "end": v(16.87, 52.7) * mm});
            skLineSegment(sketch, "E318", {"start": v(16.87, 52.7) * mm, "end": v(20.8, 52.53) * mm});
            skLineSegment(sketch, "E319", {"start": v(20.8, 52.53) * mm, "end": v(24.31, 52.1) * mm});
            skLineSegment(sketch, "E320", {"start": v(24.31, 52.1) * mm, "end": v(27.5, 51.48) * mm});
            skLineSegment(sketch, "E321", {"start": v(27.5, 51.48) * mm, "end": v(30.45, 50.72) * mm});
            skLineSegment(sketch, "E322", {"start": v(30.45, 50.72) * mm, "end": v(33.27, 49.88) * mm});
            skLineSegment(sketch, "E323", {"start": v(33.27, 49.88) * mm, "end": v(36.06, 49.02) * mm});
            skLineSegment(sketch, "E324", {"start": v(36.06, 49.02) * mm, "end": v(28.88, 47.98) * mm});
            skLineSegment(sketch, "E325", {"start": v(28.88, 47.98) * mm, "end": v(23.1, 46.07) * mm});
            skLineSegment(sketch, "E326", {"start": v(23.1, 46.07) * mm, "end": v(18.6, 43.53) * mm});
            skLineSegment(sketch, "E327", {"start": v(18.6, 43.53) * mm, "end": v(15.2, 40.57) * mm});
            skLineSegment(sketch, "E328", {"start": v(15.2, 40.57) * mm, "end": v(12.77, 37.42) * mm});
            skLineSegment(sketch, "E329", {"start": v(12.77, 37.42) * mm, "end": v(11.18, 34.3) * mm});
            skLineSegment(sketch, "E330", {"start": v(11.18, 34.3) * mm, "end": v(10.27, 31.41) * mm});
            skLineSegment(sketch, "E331", {"start": v(10.27, 31.41) * mm, "end": v(9.9, 29) * mm});
            skLineSegment(sketch, "E332", {"start": v(9.9, 29) * mm, "end": v(6.91, 29.14) * mm});
            skLineSegment(sketch, "E333", {"start": v(-8.2, 49.45) * mm, "end": v(-5.31, 50.04) * mm});
            skLineSegment(sketch, "E334", {"start": v(-5.31, 50.04) * mm, "end": v(-2.98, 50.46) * mm});
            skLineSegment(sketch, "E335", {"start": v(-2.98, 50.46) * mm, "end": v(-1.15, 50.75) * mm});
            skLineSegment(sketch, "E336", {"start": v(-1.15, 50.75) * mm, "end": v(0.22, 50.94) * mm});
            skLineSegment(sketch, "E337", {"start": v(0.22, 50.94) * mm, "end": v(1.2, 51.04) * mm});
            skLineSegment(sketch, "E338", {"start": v(1.2, 51.04) * mm, "end": v(1.83, 51.09) * mm});
            skLineSegment(sketch, "E339", {"start": v(1.83, 51.09) * mm, "end": v(2.18, 51.1) * mm});
            skLineSegment(sketch, "E340", {"start": v(2.18, 51.1) * mm, "end": v(2.28, 51.1) * mm});
            skLineSegment(sketch, "E341", {"start": v(2.28, 51.1) * mm, "end": v(2.78, 28.57) * mm});
            skLineSegment(sketch, "E342", {"start": v(2.78, 28.57) * mm, "end": v(-2.78, 27.79) * mm});
            skLineSegment(sketch, "E343", {"start": v(-2.78, 27.79) * mm, "end": v(-4.37, 32.7) * mm});
            skLineSegment(sketch, "E344", {"start": v(-4.37, 32.7) * mm, "end": v(-5.84, 37.85) * mm});
            skLineSegment(sketch, "E345", {"start": v(-5.84, 37.85) * mm, "end": v(-7.14, 43.38) * mm});
            skLineSegment(sketch, "E346", {"start": v(-7.14, 43.38) * mm, "end": v(-8.2, 49.45) * mm});
            skLineSegment(sketch, "E347", {"start": v(-12.47, 47.81) * mm, "end": v(-9.1, 37.44) * mm});
            skLineSegment(sketch, "E348", {"start": v(-9.1, 37.44) * mm, "end": v(-5.7, 26.57) * mm});
            skLineSegment(sketch, "E349", {"start": v(-5.7, 26.57) * mm, "end": v(-10.98, 24.44) * mm});
            skLineSegment(sketch, "E350", {"start": v(-10.98, 24.44) * mm, "end": v(-13.72, 28.65) * mm});
            skLineSegment(sketch, "E351", {"start": v(-13.72, 28.65) * mm, "end": v(-16.29, 33.35) * mm});
            skLineSegment(sketch, "E352", {"start": v(-16.29, 33.35) * mm, "end": v(-18.71, 38.44) * mm});
            skLineSegment(sketch, "E353", {"start": v(-18.71, 38.44) * mm, "end": v(-21.03, 43.82) * mm});
            skLineSegment(sketch, "E354", {"start": v(-21.03, 43.82) * mm, "end": v(-16.68, 46.24) * mm});
            skLineSegment(sketch, "E355", {"start": v(-16.68, 46.24) * mm, "end": v(-12.47, 47.81) * mm});
            skLineSegment(sketch, "E356", {"start": v(-25.02, 41.33) * mm, "end": v(-27.64, 40.71) * mm});
            skLineSegment(sketch, "E357", {"start": v(-27.64, 40.71) * mm, "end": v(-29.63, 39.53) * mm});
            skLineSegment(sketch, "E358", {"start": v(-29.63, 39.53) * mm, "end": v(-31.21, 37.96) * mm});
            skLineSegment(sketch, "E359", {"start": v(-31.21, 37.96) * mm, "end": v(-32.57, 36.2) * mm});
            skLineSegment(sketch, "E360", {"start": v(-32.57, 36.2) * mm, "end": v(-19.25, 20.3) * mm});
            skLineSegment(sketch, "E361", {"start": v(-19.25, 20.3) * mm, "end": v(-18.54, 20.2) * mm});
            skLineSegment(sketch, "E362", {"start": v(-18.54, 20.2) * mm, "end": v(-18.02, 20.17) * mm});
            skLineSegment(sketch, "E363", {"start": v(-18.02, 20.17) * mm, "end": v(-17.6, 20.16) * mm});
            skLineSegment(sketch, "E364", {"start": v(-17.6, 20.16) * mm, "end": v(-17.18, 20.16) * mm});
            skLineSegment(sketch, "E365", {"start": v(-17.18, 20.16) * mm, "end": v(-13.9, 22.51) * mm});
            skLineSegment(sketch, "E366", {"start": v(-13.9, 22.51) * mm, "end": v(-16.63, 26.88) * mm});
            skLineSegment(sketch, "E367", {"start": v(-16.63, 26.88) * mm, "end": v(-19.33, 31.16) * mm});
            skLineSegment(sketch, "E368", {"start": v(-19.33, 31.16) * mm, "end": v(-22.1, 35.82) * mm});
            skLineSegment(sketch, "E369", {"start": v(-22.1, 35.82) * mm, "end": v(-25.02, 41.33) * mm});
            skLineSegment(sketch, "E370", {"start": v(-41.7, 26.72) * mm, "end": v(-40.56, 28.53) * mm});
            skLineSegment(sketch, "E371", {"start": v(-40.56, 28.53) * mm, "end": v(-39.26, 30.31) * mm});
            skLineSegment(sketch, "E372", {"start": v(-39.26, 30.31) * mm, "end": v(-37.65, 32.03) * mm});
            skLineSegment(sketch, "E373", {"start": v(-37.65, 32.03) * mm, "end": v(-35.57, 33.63) * mm});
            skLineSegment(sketch, "E374", {"start": v(-35.57, 33.63) * mm, "end": v(-21.03, 18.02) * mm});
            skLineSegment(sketch, "E375", {"start": v(-21.03, 18.02) * mm, "end": v(-21.7, 16.85) * mm});
            skLineSegment(sketch, "E376", {"start": v(-21.7, 16.85) * mm, "end": v(-22.8, 15.81) * mm});
            skLineSegment(sketch, "E377", {"start": v(-22.8, 15.81) * mm, "end": v(-24.1, 14.53) * mm});
            skLineSegment(sketch, "E378", {"start": v(-24.1, 14.53) * mm, "end": v(-41.7, 26.72) * mm});
            skLineSegment(sketch, "E379", {"start": v(-44.76, 23.65) * mm, "end": v(-47.47, 20.02) * mm});
            skLineSegment(sketch, "E380", {"start": v(-47.47, 20.02) * mm, "end": v(-49.04, 15.95) * mm});
            skLineSegment(sketch, "E381", {"start": v(-49.04, 15.95) * mm, "end": v(-44.05, 13.7) * mm});
            skLineSegment(sketch, "E382", {"start": v(-44.05, 13.7) * mm, "end": v(-39.14, 11.5) * mm});
            skLineSegment(sketch, "E383", {"start": v(-39.14, 11.5) * mm, "end": v(-34.6, 9.52) * mm});
            skLineSegment(sketch, "E384", {"start": v(-34.6, 9.52) * mm, "end": v(-30.72, 7.97) * mm});
            skLineSegment(sketch, "E385", {"start": v(-30.72, 7.97) * mm, "end": v(-30.5, 8.38) * mm});
            skLineSegment(sketch, "E386", {"start": v(-30.5, 8.38) * mm, "end": v(-30.3, 8.74) * mm});
            skLineSegment(sketch, "E387", {"start": v(-30.3, 8.74) * mm, "end": v(-30.1, 9.1) * mm});
            skLineSegment(sketch, "E388", {"start": v(-30.1, 9.1) * mm, "end": v(-29.87, 9.5) * mm});
            skLineSegment(sketch, "E389", {"start": v(-29.87, 9.5) * mm, "end": v(-29.6, 10) * mm});
            skLineSegment(sketch, "E390", {"start": v(-29.6, 10) * mm, "end": v(-29.28, 10.62) * mm});
            skLineSegment(sketch, "E391", {"start": v(-29.28, 10.62) * mm, "end": v(-28.88, 11.43) * mm});
            skLineSegment(sketch, "E392", {"start": v(-28.88, 11.43) * mm, "end": v(-28.37, 12.46) * mm});
            skLineSegment(sketch, "E393", {"start": v(-28.37, 12.46) * mm, "end": v(-32.2, 15.16) * mm});
            skLineSegment(sketch, "E394", {"start": v(-32.2, 15.16) * mm, "end": v(-36.04, 17.86) * mm});
            skLineSegment(sketch, "E395", {"start": v(-36.04, 17.86) * mm, "end": v(-40.14, 20.66) * mm});
            skLineSegment(sketch, "E396", {"start": v(-40.14, 20.66) * mm, "end": v(-44.76, 23.65) * mm});
            skLineSegment(sketch, "E397", {"start": v(-53.81, 4.48) * mm, "end": v(-53.63, 5.55) * mm});
            skLineSegment(sketch, "E398", {"start": v(-53.63, 5.55) * mm, "end": v(-53.43, 6.64) * mm});
            skLineSegment(sketch, "E399", {"start": v(-53.43, 6.64) * mm, "end": v(-53.07, 7.86) * mm});
            skLineSegment(sketch, "E400", {"start": v(-53.07, 7.86) * mm, "end": v(-52.39, 9.33) * mm});
            skLineSegment(sketch, "E401", {"start": v(-52.39, 9.33) * mm, "end": v(-50.68, 12.18) * mm});
            skLineSegment(sketch, "E402", {"start": v(-50.68, 12.18) * mm, "end": v(-43.98, 9.54) * mm});
            skLineSegment(sketch, "E403", {"start": v(-43.98, 9.54) * mm, "end": v(-40.46, 8.43) * mm});
            skLineSegment(sketch, "E404", {"start": v(-40.46, 8.43) * mm, "end": v(-37.62, 7.37) * mm});
            skLineSegment(sketch, "E405", {"start": v(-37.62, 7.37) * mm, "end": v(-35.23, 6.34) * mm});
            skLineSegment(sketch, "E406", {"start": v(-35.23, 6.34) * mm, "end": v(-33.07, 5.34) * mm});
            skLineSegment(sketch, "E407", {"start": v(-33.07, 5.34) * mm, "end": v(-33.25, 4.5) * mm});
            skLineSegment(sketch, "E408", {"start": v(-33.25, 4.5) * mm, "end": v(-33.47, 3.62) * mm});
            skLineSegment(sketch, "E409", {"start": v(-33.47, 3.62) * mm, "end": v(-33.84, 2.6) * mm});
            skLineSegment(sketch, "E410", {"start": v(-33.84, 2.6) * mm, "end": v(-34.43, 1.34) * mm});
            skLineSegment(sketch, "E411", {"start": v(-34.43, 1.34) * mm, "end": v(-53.81, 4.48) * mm});
            skSolve(sketch);
        }
        {
            var Q0;
            Q0=makeQuery(id+"F0.imprint","IMPRINT",FACE,{"disambiguationData":[TD([[makeQuery(id+"F0.imprint","IMPRINT",EDGE,{"derivedFrom":sQuery(id+"F0.wireOp",EDGE,"E130")}),-1.0]])]});
            var Q1;
            Q1=makeQuery(id+"F0.imprint","IMPRINT",FACE,{"disambiguationData":[TD([[makeQuery(id+"F0.imprint","IMPRINT",EDGE,{"derivedFrom":sQuery(id+"F0.wireOp",EDGE,"E115")}),-1.0]])]});
            var Q2;
            Q2=makeQuery(id+"F0.imprint","IMPRINT",FACE,{"disambiguationData":[TD([[makeQuery(id+"F0.imprint","IMPRINT",EDGE,{"derivedFrom":sQuery(id+"F0.wireOp",EDGE,"E397")}),-1.0]])]});
            var Q3;
            Q3=makeQuery(id+"F0.imprint","IMPRINT",FACE,{"disambiguationData":[TD([[makeQuery(id+"F0.imprint","IMPRINT",EDGE,{"derivedFrom":sQuery(id+"F0.wireOp",EDGE,"E379")}),1.0]])]});
            var Q4;
            Q4=makeQuery(id+"F0.imprint","IMPRINT",FACE,{"disambiguationData":[TD([[makeQuery(id+"F0.imprint","IMPRINT",EDGE,{"derivedFrom":sQuery(id+"F0.wireOp",EDGE,"E370")}),-1.0]])]});
            var Q5;
            Q5=makeQuery(id+"F0.imprint","IMPRINT",FACE,{"disambiguationData":[TD([[makeQuery(id+"F0.imprint","IMPRINT",EDGE,{"derivedFrom":sQuery(id+"F0.wireOp",EDGE,"E356")}),1.0]])]});
            var Q6;
            Q6=makeQuery(id+"F0.imprint","IMPRINT",FACE,{"disambiguationData":[TD([[makeQuery(id+"F0.imprint","IMPRINT",EDGE,{"derivedFrom":sQuery(id+"F0.wireOp",EDGE,"E347")}),-1.0]])]});
            var Q7;
            Q7=makeQuery(id+"F0.imprint","IMPRINT",FACE,{"disambiguationData":[TD([[makeQuery(id+"F0.imprint","IMPRINT",EDGE,{"derivedFrom":sQuery(id+"F0.wireOp",EDGE,"E333")}),-1.0]])]});
            var Q8;
            Q8=makeQuery(id+"F0.imprint","IMPRINT",FACE,{"disambiguationData":[TD([[makeQuery(id+"F0.imprint","IMPRINT",EDGE,{"derivedFrom":sQuery(id+"F0.wireOp",EDGE,"E312")}),-1.0]])]});
            var Q9;
            Q9=makeQuery(id+"F0.imprint","IMPRINT",FACE,{"disambiguationData":[TD([[makeQuery(id+"F0.imprint","IMPRINT",EDGE,{"derivedFrom":sQuery(id+"F0.wireOp",EDGE,"E0")}),-1.0]])]});
            extrude(context, id + "F1", {"entities" : qUnion([Q0, Q1, Q2, Q3, Q4, Q5, Q6, Q7, Q8, Q9]), "depth" : 25.4 * mm});
        }
        {
            var Q0;
            Q0=makeQuery(id+"F1.opExtrude","CAP_FACE",FACE,{"disambiguationData":[OSD([sQuery(id+"F0.wireOp",EDGE,"E130"),sQuery(id+"F0.wireOp",EDGE,"E131"),sQuery(id+"F0.wireOp",EDGE,"E132"),sQuery(id+"F0.wireOp",EDGE,"E133"),sQuery(id+"F0.wireOp",EDGE,"E134"),sQuery(id+"F0.wireOp",EDGE,"E135"),sQuery(id+"F0.wireOp",EDGE,"E136"),sQuery(id+"F0.wireOp",EDGE,"E137"),sQuery(id+"F0.wireOp",EDGE,"E138"),sQuery(id+"F0.wireOp",EDGE,"E139"),sQuery(id+"F0.wireOp",EDGE,"E140"),sQuery(id+"F0.wireOp",EDGE,"E141"),sQuery(id+"F0.wireOp",EDGE,"E142"),sQuery(id+"F0.wireOp",EDGE,"E143"),sQuery(id+"F0.wireOp",EDGE,"E144"),sQuery(id+"F0.wireOp",EDGE,"E145"),sQuery(id+"F0.wireOp",EDGE,"E146"),sQuery(id+"F0.wireOp",EDGE,"E147"),sQuery(id+"F0.wireOp",EDGE,"E148"),sQuery(id+"F0.wireOp",EDGE,"E149"),sQuery(id+"F0.wireOp",EDGE,"E150"),sQuery(id+"F0.wireOp",EDGE,"E151"),sQuery(id+"F0.wireOp",EDGE,"E152"),sQuery(id+"F0.wireOp",EDGE,"E153"),sQuery(id+"F0.wireOp",EDGE,"E154"),sQuery(id+"F0.wireOp",EDGE,"E155"),sQuery(id+"F0.wireOp",EDGE,"E156"),sQuery(id+"F0.wireOp",EDGE,"E157"),sQuery(id+"F0.wireOp",EDGE,"E158"),sQuery(id+"F0.wireOp",EDGE,"E159"),sQuery(id+"F0.wireOp",EDGE,"E160"),sQuery(id+"F0.wireOp",EDGE,"E161"),sQuery(id+"F0.wireOp",EDGE,"E162"),sQuery(id+"F0.wireOp",EDGE,"E163"),sQuery(id+"F0.wireOp",EDGE,"E164"),sQuery(id+"F0.wireOp",EDGE,"E165"),sQuery(id+"F0.wireOp",EDGE,"E166"),sQuery(id+"F0.wireOp",EDGE,"E167"),sQuery(id+"F0.wireOp",EDGE,"E168"),sQuery(id+"F0.wireOp",EDGE,"E169"),sQuery(id+"F0.wireOp",EDGE,"E170"),sQuery(id+"F0.wireOp",EDGE,"E171"),sQuery(id+"F0.wireOp",EDGE,"E172"),sQuery(id+"F0.wireOp",EDGE,"E173"),sQuery(id+"F0.wireOp",EDGE,"E174"),sQuery(id+"F0.wireOp",EDGE,"E175"),sQuery(id+"F0.wireOp",EDGE,"E176"),sQuery(id+"F0.wireOp",EDGE,"E177"),sQuery(id+"F0.wireOp",EDGE,"E178"),sQuery(id+"F0.wireOp",EDGE,"E179"),sQuery(id+"F0.wireOp",EDGE,"E180"),sQuery(id+"F0.wireOp",EDGE,"E181"),sQuery(id+"F0.wireOp",EDGE,"E182"),sQuery(id+"F0.wireOp",EDGE,"E183"),sQuery(id+"F0.wireOp",EDGE,"E184"),sQuery(id+"F0.wireOp",EDGE,"E185"),sQuery(id+"F0.wireOp",EDGE,"E186"),sQuery(id+"F0.wireOp",EDGE,"E187"),sQuery(id+"F0.wireOp",EDGE,"E188"),sQuery(id+"F0.wireOp",EDGE,"E189"),sQuery(id+"F0.wireOp",EDGE,"E190"),sQuery(id+"F0.wireOp",EDGE,"E191"),sQuery(id+"F0.wireOp",EDGE,"E192"),sQuery(id+"F0.wireOp",EDGE,"E193"),sQuery(id+"F0.wireOp",EDGE,"E194"),sQuery(id+"F0.wireOp",EDGE,"E195"),sQuery(id+"F0.wireOp",EDGE,"E196"),sQuery(id+"F0.wireOp",EDGE,"E197"),sQuery(id+"F0.wireOp",EDGE,"E198"),sQuery(id+"F0.wireOp",EDGE,"E199"),sQuery(id+"F0.wireOp",EDGE,"E200"),sQuery(id+"F0.wireOp",EDGE,"E201"),sQuery(id+"F0.wireOp",EDGE,"E202"),sQuery(id+"F0.wireOp",EDGE,"E203"),sQuery(id+"F0.wireOp",EDGE,"E204"),sQuery(id+"F0.wireOp",EDGE,"E205"),sQuery(id+"F0.wireOp",EDGE,"E206"),sQuery(id+"F0.wireOp",EDGE,"E207"),sQuery(id+"F0.wireOp",EDGE,"E208"),sQuery(id+"F0.wireOp",EDGE,"E209"),sQuery(id+"F0.wireOp",EDGE,"E210"),sQuery(id+"F0.wireOp",EDGE,"E211"),sQuery(id+"F0.wireOp",EDGE,"E212"),sQuery(id+"F0.wireOp",EDGE,"E213"),sQuery(id+"F0.wireOp",EDGE,"E214"),sQuery(id+"F0.wireOp",EDGE,"E215"),sQuery(id+"F0.wireOp",EDGE,"E216"),sQuery(id+"F0.wireOp",EDGE,"E217"),sQuery(id+"F0.wireOp",EDGE,"E218"),sQuery(id+"F0.wireOp",EDGE,"E219"),sQuery(id+"F0.wireOp",EDGE,"E220"),sQuery(id+"F0.wireOp",EDGE,"E221"),sQuery(id+"F0.wireOp",EDGE,"E222"),sQuery(id+"F0.wireOp",EDGE,"E223"),sQuery(id+"F0.wireOp",EDGE,"E224"),sQuery(id+"F0.wireOp",EDGE,"E225"),sQuery(id+"F0.wireOp",EDGE,"E226"),sQuery(id+"F0.wireOp",EDGE,"E227"),sQuery(id+"F0.wireOp",EDGE,"E228"),sQuery(id+"F0.wireOp",EDGE,"E229"),sQuery(id+"F0.wireOp",EDGE,"E230"),sQuery(id+"F0.wireOp",EDGE,"E231"),sQuery(id+"F0.wireOp",EDGE,"E232"),sQuery(id+"F0.wireOp",EDGE,"E233"),sQuery(id+"F0.wireOp",EDGE,"E234"),sQuery(id+"F0.wireOp",EDGE,"E235"),sQuery(id+"F0.wireOp",EDGE,"E236"),sQuery(id+"F0.wireOp",EDGE,"E237"),sQuery(id+"F0.wireOp",EDGE,"E238"),sQuery(id+"F0.wireOp",EDGE,"E239"),sQuery(id+"F0.wireOp",EDGE,"E240"),sQuery(id+"F0.wireOp",EDGE,"E241"),sQuery(id+"F0.wireOp",EDGE,"E242"),sQuery(id+"F0.wireOp",EDGE,"E243"),sQuery(id+"F0.wireOp",EDGE,"E244"),sQuery(id+"F0.wireOp",EDGE,"E245"),sQuery(id+"F0.wireOp",EDGE,"E246"),sQuery(id+"F0.wireOp",EDGE,"E247"),sQuery(id+"F0.wireOp",EDGE,"E248"),sQuery(id+"F0.wireOp",EDGE,"E249"),sQuery(id+"F0.wireOp",EDGE,"E250"),sQuery(id+"F0.wireOp",EDGE,"E251"),sQuery(id+"F0.wireOp",EDGE,"E252"),sQuery(id+"F0.wireOp",EDGE,"E253"),sQuery(id+"F0.wireOp",EDGE,"E254"),sQuery(id+"F0.wireOp",EDGE,"E255"),sQuery(id+"F0.wireOp",EDGE,"E256"),sQuery(id+"F0.wireOp",EDGE,"E257"),sQuery(id+"F0.wireOp",EDGE,"E258"),sQuery(id+"F0.wireOp",EDGE,"E259"),sQuery(id+"F0.wireOp",EDGE,"E260"),sQuery(id+"F0.wireOp",EDGE,"E261"),sQuery(id+"F0.wireOp",EDGE,"E262"),sQuery(id+"F0.wireOp",EDGE,"E263"),sQuery(id+"F0.wireOp",EDGE,"E264"),sQuery(id+"F0.wireOp",EDGE,"E265"),sQuery(id+"F0.wireOp",EDGE,"E266"),sQuery(id+"F0.wireOp",EDGE,"E267"),sQuery(id+"F0.wireOp",EDGE,"E268"),sQuery(id+"F0.wireOp",EDGE,"E269"),sQuery(id+"F0.wireOp",EDGE,"E270"),sQuery(id+"F0.wireOp",EDGE,"E271"),sQuery(id+"F0.wireOp",EDGE,"E272"),sQuery(id+"F0.wireOp",EDGE,"E273"),sQuery(id+"F0.wireOp",EDGE,"E274"),sQuery(id+"F0.wireOp",EDGE,"E275"),sQuery(id+"F0.wireOp",EDGE,"E276"),sQuery(id+"F0.wireOp",EDGE,"E277"),sQuery(id+"F0.wireOp",EDGE,"E278"),sQuery(id+"F0.wireOp",EDGE,"E279"),sQuery(id+"F0.wireOp",EDGE,"E280"),sQuery(id+"F0.wireOp",EDGE,"E281"),sQuery(id+"F0.wireOp",EDGE,"E282"),sQuery(id+"F0.wireOp",EDGE,"E283"),sQuery(id+"F0.wireOp",EDGE,"E284"),sQuery(id+"F0.wireOp",EDGE,"E285"),sQuery(id+"F0.wireOp",EDGE,"E286"),sQuery(id+"F0.wireOp",EDGE,"E287"),sQuery(id+"F0.wireOp",EDGE,"E288"),sQuery(id+"F0.wireOp",EDGE,"E289"),sQuery(id+"F0.wireOp",EDGE,"E290"),sQuery(id+"F0.wireOp",EDGE,"E291"),sQuery(id+"F0.wireOp",EDGE,"E292"),sQuery(id+"F0.wireOp",EDGE,"E293"),sQuery(id+"F0.wireOp",EDGE,"E294"),sQuery(id+"F0.wireOp",EDGE,"E295"),sQuery(id+"F0.wireOp",EDGE,"E296"),sQuery(id+"F0.wireOp",EDGE,"E297"),sQuery(id+"F0.wireOp",EDGE,"E298"),sQuery(id+"F0.wireOp",EDGE,"E299"),sQuery(id+"F0.wireOp",EDGE,"E300"),sQuery(id+"F0.wireOp",EDGE,"E301"),sQuery(id+"F0.wireOp",EDGE,"E302"),sQuery(id+"F0.wireOp",EDGE,"E303"),sQuery(id+"F0.wireOp",EDGE,"E304"),sQuery(id+"F0.wireOp",EDGE,"E305"),sQuery(id+"F0.wireOp",EDGE,"E306"),sQuery(id+"F0.wireOp",EDGE,"E307"),sQuery(id+"F0.wireOp",EDGE,"E308"),sQuery(id+"F0.wireOp",EDGE,"E309"),sQuery(id+"F0.wireOp",EDGE,"E310"),sQuery(id+"F0.wireOp",EDGE,"E311")])],"isStart":true});
            var sketch = newSketch(context, id + "F2", { "sketchPlane" : qUnion([Q0])});
            skCircle(sketch, "E412", {"center": v(0, 0) * mm, "radius": 133.76 * mm});
            skSolve(sketch);
        }
        {
            var Q0;
            Q0 = qSketchRegion(id + "F2", true);
            extrude(context, id + "F3", {"entities" : qUnion([Q0]), "depth" : 11.6 * mm, "hasSecondDirection" : true, "secondDirectionOppositeDirection" : true, "secondDirectionDepth" : 3.8 * mm});
        }
        {
            var Q0;
            Q0=makeQuery(id+"F1.opExtrude","SWEPT_BODY",BODY,{"disambiguationData":[OSD([sQuery(id+"F0.wireOp",EDGE,"E0"),sQuery(id+"F0.wireOp",EDGE,"E1"),sQuery(id+"F0.wireOp",EDGE,"E2"),sQuery(id+"F0.wireOp",EDGE,"E3"),sQuery(id+"F0.wireOp",EDGE,"E4"),sQuery(id+"F0.wireOp",EDGE,"E5"),sQuery(id+"F0.wireOp",EDGE,"E6"),sQuery(id+"F0.wireOp",EDGE,"E7"),sQuery(id+"F0.wireOp",EDGE,"E8"),sQuery(id+"F0.wireOp",EDGE,"E9"),sQuery(id+"F0.wireOp",EDGE,"E10"),sQuery(id+"F0.wireOp",EDGE,"E11"),sQuery(id+"F0.wireOp",EDGE,"E12"),sQuery(id+"F0.wireOp",EDGE,"E13"),sQuery(id+"F0.wireOp",EDGE,"E14"),sQuery(id+"F0.wireOp",EDGE,"E15"),sQuery(id+"F0.wireOp",EDGE,"E16"),sQuery(id+"F0.wireOp",EDGE,"E17"),sQuery(id+"F0.wireOp",EDGE,"E18"),sQuery(id+"F0.wireOp",EDGE,"E19"),sQuery(id+"F0.wireOp",EDGE,"E20"),sQuery(id+"F0.wireOp",EDGE,"E21"),sQuery(id+"F0.wireOp",EDGE,"E22"),sQuery(id+"F0.wireOp",EDGE,"E23"),sQuery(id+"F0.wireOp",EDGE,"E24"),sQuery(id+"F0.wireOp",EDGE,"E25"),sQuery(id+"F0.wireOp",EDGE,"E26"),sQuery(id+"F0.wireOp",EDGE,"E27"),sQuery(id+"F0.wireOp",EDGE,"E28"),sQuery(id+"F0.wireOp",EDGE,"E29"),sQuery(id+"F0.wireOp",EDGE,"E30"),sQuery(id+"F0.wireOp",EDGE,"E31"),sQuery(id+"F0.wireOp",EDGE,"E32"),sQuery(id+"F0.wireOp",EDGE,"E33"),sQuery(id+"F0.wireOp",EDGE,"E34"),sQuery(id+"F0.wireOp",EDGE,"E35"),sQuery(id+"F0.wireOp",EDGE,"E36"),sQuery(id+"F0.wireOp",EDGE,"E37"),sQuery(id+"F0.wireOp",EDGE,"E38"),sQuery(id+"F0.wireOp",EDGE,"E39"),sQuery(id+"F0.wireOp",EDGE,"E40"),sQuery(id+"F0.wireOp",EDGE,"E41"),sQuery(id+"F0.wireOp",EDGE,"E42"),sQuery(id+"F0.wireOp",EDGE,"E43"),sQuery(id+"F0.wireOp",EDGE,"E44"),sQuery(id+"F0.wireOp",EDGE,"E45"),sQuery(id+"F0.wireOp",EDGE,"E46"),sQuery(id+"F0.wireOp",EDGE,"E47"),sQuery(id+"F0.wireOp",EDGE,"E48"),sQuery(id+"F0.wireOp",EDGE,"E49"),sQuery(id+"F0.wireOp",EDGE,"E50"),sQuery(id+"F0.wireOp",EDGE,"E51"),sQuery(id+"F0.wireOp",EDGE,"E52"),sQuery(id+"F0.wireOp",EDGE,"E53"),sQuery(id+"F0.wireOp",EDGE,"E54"),sQuery(id+"F0.wireOp",EDGE,"E55"),sQuery(id+"F0.wireOp",EDGE,"E56"),sQuery(id+"F0.wireOp",EDGE,"E57"),sQuery(id+"F0.wireOp",EDGE,"E58"),sQuery(id+"F0.wireOp",EDGE,"E59"),sQuery(id+"F0.wireOp",EDGE,"E60"),sQuery(id+"F0.wireOp",EDGE,"E61"),sQuery(id+"F0.wireOp",EDGE,"E62"),sQuery(id+"F0.wireOp",EDGE,"E63"),sQuery(id+"F0.wireOp",EDGE,"E64"),sQuery(id+"F0.wireOp",EDGE,"E65"),sQuery(id+"F0.wireOp",EDGE,"E66"),sQuery(id+"F0.wireOp",EDGE,"E67"),sQuery(id+"F0.wireOp",EDGE,"E68"),sQuery(id+"F0.wireOp",EDGE,"E69"),sQuery(id+"F0.wireOp",EDGE,"E70"),sQuery(id+"F0.wireOp",EDGE,"E71"),sQuery(id+"F0.wireOp",EDGE,"E72"),sQuery(id+"F0.wireOp",EDGE,"E73"),sQuery(id+"F0.wireOp",EDGE,"E74"),sQuery(id+"F0.wireOp",EDGE,"E75"),sQuery(id+"F0.wireOp",EDGE,"E76"),sQuery(id+"F0.wireOp",EDGE,"E77"),sQuery(id+"F0.wireOp",EDGE,"E78"),sQuery(id+"F0.wireOp",EDGE,"E79"),sQuery(id+"F0.wireOp",EDGE,"E80"),sQuery(id+"F0.wireOp",EDGE,"E81"),sQuery(id+"F0.wireOp",EDGE,"E82"),sQuery(id+"F0.wireOp",EDGE,"E83"),sQuery(id+"F0.wireOp",EDGE,"E84"),sQuery(id+"F0.wireOp",EDGE,"E85"),sQuery(id+"F0.wireOp",EDGE,"E86"),sQuery(id+"F0.wireOp",EDGE,"E87"),sQuery(id+"F0.wireOp",EDGE,"E88"),sQuery(id+"F0.wireOp",EDGE,"E89"),sQuery(id+"F0.wireOp",EDGE,"E90"),sQuery(id+"F0.wireOp",EDGE,"E91"),sQuery(id+"F0.wireOp",EDGE,"E92"),sQuery(id+"F0.wireOp",EDGE,"E93"),sQuery(id+"F0.wireOp",EDGE,"E94"),sQuery(id+"F0.wireOp",EDGE,"E95"),sQuery(id+"F0.wireOp",EDGE,"E96"),sQuery(id+"F0.wireOp",EDGE,"E97"),sQuery(id+"F0.wireOp",EDGE,"E98"),sQuery(id+"F0.wireOp",EDGE,"E99"),sQuery(id+"F0.wireOp",EDGE,"E100"),sQuery(id+"F0.wireOp",EDGE,"E101"),sQuery(id+"F0.wireOp",EDGE,"E102"),sQuery(id+"F0.wireOp",EDGE,"E103"),sQuery(id+"F0.wireOp",EDGE,"E104"),sQuery(id+"F0.wireOp",EDGE,"E105"),sQuery(id+"F0.wireOp",EDGE,"E106"),sQuery(id+"F0.wireOp",EDGE,"E107"),sQuery(id+"F0.wireOp",EDGE,"E108"),sQuery(id+"F0.wireOp",EDGE,"E109"),sQuery(id+"F0.wireOp",EDGE,"E110"),sQuery(id+"F0.wireOp",EDGE,"E111"),sQuery(id+"F0.wireOp",EDGE,"E112"),sQuery(id+"F0.wireOp",EDGE,"E113"),sQuery(id+"F0.wireOp",EDGE,"E114")])]});
            var Q1;
            Q1=makeQuery(id+"F1.opExtrude","SWEPT_BODY",BODY,{"disambiguationData":[OSD([sQuery(id+"F0.wireOp",EDGE,"E379"),sQuery(id+"F0.wireOp",EDGE,"E380"),sQuery(id+"F0.wireOp",EDGE,"E381"),sQuery(id+"F0.wireOp",EDGE,"E382"),sQuery(id+"F0.wireOp",EDGE,"E383"),sQuery(id+"F0.wireOp",EDGE,"E384"),sQuery(id+"F0.wireOp",EDGE,"E385"),sQuery(id+"F0.wireOp",EDGE,"E386"),sQuery(id+"F0.wireOp",EDGE,"E387"),sQuery(id+"F0.wireOp",EDGE,"E388"),sQuery(id+"F0.wireOp",EDGE,"E389"),sQuery(id+"F0.wireOp",EDGE,"E390"),sQuery(id+"F0.wireOp",EDGE,"E391"),sQuery(id+"F0.wireOp",EDGE,"E392"),sQuery(id+"F0.wireOp",EDGE,"E393"),sQuery(id+"F0.wireOp",EDGE,"E394"),sQuery(id+"F0.wireOp",EDGE,"E395"),sQuery(id+"F0.wireOp",EDGE,"E396")])]});
            var Q2;
            Q2=makeQuery(id+"F1.opExtrude","SWEPT_BODY",BODY,{"disambiguationData":[OSD([sQuery(id+"F0.wireOp",EDGE,"E397"),sQuery(id+"F0.wireOp",EDGE,"E398"),sQuery(id+"F0.wireOp",EDGE,"E399"),sQuery(id+"F0.wireOp",EDGE,"E400"),sQuery(id+"F0.wireOp",EDGE,"E401"),sQuery(id+"F0.wireOp",EDGE,"E402"),sQuery(id+"F0.wireOp",EDGE,"E403"),sQuery(id+"F0.wireOp",EDGE,"E404"),sQuery(id+"F0.wireOp",EDGE,"E405"),sQuery(id+"F0.wireOp",EDGE,"E406"),sQuery(id+"F0.wireOp",EDGE,"E407"),sQuery(id+"F0.wireOp",EDGE,"E408"),sQuery(id+"F0.wireOp",EDGE,"E409"),sQuery(id+"F0.wireOp",EDGE,"E410"),sQuery(id+"F0.wireOp",EDGE,"E411")])]});
            var Q3;
            Q3=makeQuery(id+"F1.opExtrude","SWEPT_BODY",BODY,{"disambiguationData":[OSD([sQuery(id+"F0.wireOp",EDGE,"E115"),sQuery(id+"F0.wireOp",EDGE,"E116"),sQuery(id+"F0.wireOp",EDGE,"E117"),sQuery(id+"F0.wireOp",EDGE,"E118"),sQuery(id+"F0.wireOp",EDGE,"E119"),sQuery(id+"F0.wireOp",EDGE,"E120"),sQuery(id+"F0.wireOp",EDGE,"E121"),sQuery(id+"F0.wireOp",EDGE,"E122"),sQuery(id+"F0.wireOp",EDGE,"E123"),sQuery(id+"F0.wireOp",EDGE,"E124"),sQuery(id+"F0.wireOp",EDGE,"E125"),sQuery(id+"F0.wireOp",EDGE,"E126"),sQuery(id+"F0.wireOp",EDGE,"E127"),sQuery(id+"F0.wireOp",EDGE,"E128"),sQuery(id+"F0.wireOp",EDGE,"E129")])]});
            var Q4;
            Q4=makeQuery(id+"F1.opExtrude","SWEPT_BODY",BODY,{"disambiguationData":[OSD([sQuery(id+"F0.wireOp",EDGE,"E370"),sQuery(id+"F0.wireOp",EDGE,"E371"),sQuery(id+"F0.wireOp",EDGE,"E372"),sQuery(id+"F0.wireOp",EDGE,"E373"),sQuery(id+"F0.wireOp",EDGE,"E374"),sQuery(id+"F0.wireOp",EDGE,"E375"),sQuery(id+"F0.wireOp",EDGE,"E376"),sQuery(id+"F0.wireOp",EDGE,"E377"),sQuery(id+"F0.wireOp",EDGE,"E378")])]});
            var Q5;
            Q5=makeQuery(id+"F1.opExtrude","SWEPT_BODY",BODY,{"disambiguationData":[OSD([sQuery(id+"F0.wireOp",EDGE,"E356"),sQuery(id+"F0.wireOp",EDGE,"E357"),sQuery(id+"F0.wireOp",EDGE,"E358"),sQuery(id+"F0.wireOp",EDGE,"E359"),sQuery(id+"F0.wireOp",EDGE,"E360"),sQuery(id+"F0.wireOp",EDGE,"E361"),sQuery(id+"F0.wireOp",EDGE,"E362"),sQuery(id+"F0.wireOp",EDGE,"E363"),sQuery(id+"F0.wireOp",EDGE,"E364"),sQuery(id+"F0.wireOp",EDGE,"E365"),sQuery(id+"F0.wireOp",EDGE,"E366"),sQuery(id+"F0.wireOp",EDGE,"E367"),sQuery(id+"F0.wireOp",EDGE,"E368"),sQuery(id+"F0.wireOp",EDGE,"E369")])]});
            var Q6;
            Q6=makeQuery(id+"F1.opExtrude","SWEPT_BODY",BODY,{"disambiguationData":[OSD([sQuery(id+"F0.wireOp",EDGE,"E347"),sQuery(id+"F0.wireOp",EDGE,"E348"),sQuery(id+"F0.wireOp",EDGE,"E349"),sQuery(id+"F0.wireOp",EDGE,"E350"),sQuery(id+"F0.wireOp",EDGE,"E351"),sQuery(id+"F0.wireOp",EDGE,"E352"),sQuery(id+"F0.wireOp",EDGE,"E353"),sQuery(id+"F0.wireOp",EDGE,"E354"),sQuery(id+"F0.wireOp",EDGE,"E355")])]});
            var Q7;
            Q7=makeQuery(id+"F1.opExtrude","SWEPT_BODY",BODY,{"disambiguationData":[OSD([sQuery(id+"F0.wireOp",EDGE,"E333"),sQuery(id+"F0.wireOp",EDGE,"E334"),sQuery(id+"F0.wireOp",EDGE,"E335"),sQuery(id+"F0.wireOp",EDGE,"E336"),sQuery(id+"F0.wireOp",EDGE,"E337"),sQuery(id+"F0.wireOp",EDGE,"E338"),sQuery(id+"F0.wireOp",EDGE,"E339"),sQuery(id+"F0.wireOp",EDGE,"E340"),sQuery(id+"F0.wireOp",EDGE,"E341"),sQuery(id+"F0.wireOp",EDGE,"E342"),sQuery(id+"F0.wireOp",EDGE,"E343"),sQuery(id+"F0.wireOp",EDGE,"E344"),sQuery(id+"F0.wireOp",EDGE,"E345"),sQuery(id+"F0.wireOp",EDGE,"E346")])]});
            var Q8;
            Q8=makeQuery(id+"F1.opExtrude","SWEPT_BODY",BODY,{"disambiguationData":[OSD([sQuery(id+"F0.wireOp",EDGE,"E312"),sQuery(id+"F0.wireOp",EDGE,"E313"),sQuery(id+"F0.wireOp",EDGE,"E314"),sQuery(id+"F0.wireOp",EDGE,"E315"),sQuery(id+"F0.wireOp",EDGE,"E316"),sQuery(id+"F0.wireOp",EDGE,"E317"),sQuery(id+"F0.wireOp",EDGE,"E318"),sQuery(id+"F0.wireOp",EDGE,"E319"),sQuery(id+"F0.wireOp",EDGE,"E320"),sQuery(id+"F0.wireOp",EDGE,"E321"),sQuery(id+"F0.wireOp",EDGE,"E322"),sQuery(id+"F0.wireOp",EDGE,"E323"),sQuery(id+"F0.wireOp",EDGE,"E324"),sQuery(id+"F0.wireOp",EDGE,"E325"),sQuery(id+"F0.wireOp",EDGE,"E326"),sQuery(id+"F0.wireOp",EDGE,"E327"),sQuery(id+"F0.wireOp",EDGE,"E328"),sQuery(id+"F0.wireOp",EDGE,"E329"),sQuery(id+"F0.wireOp",EDGE,"E330"),sQuery(id+"F0.wireOp",EDGE,"E331"),sQuery(id+"F0.wireOp",EDGE,"E332")])]});
            var Q9;
            Q9=makeQuery(id+"F3.opExtrude","SWEPT_BODY",BODY,{"disambiguationData":[OSD([sQuery(id+"F2.wireOp",EDGE,"E412")])]});
            var Q10;
            Q10=makeQuery(id+"F1.opExtrude","SWEPT_BODY",BODY,{"disambiguationData":[OSD([sQuery(id+"F0.wireOp",EDGE,"E130"),sQuery(id+"F0.wireOp",EDGE,"E131"),sQuery(id+"F0.wireOp",EDGE,"E132"),sQuery(id+"F0.wireOp",EDGE,"E133"),sQuery(id+"F0.wireOp",EDGE,"E134"),sQuery(id+"F0.wireOp",EDGE,"E135"),sQuery(id+"F0.wireOp",EDGE,"E136"),sQuery(id+"F0.wireOp",EDGE,"E137"),sQuery(id+"F0.wireOp",EDGE,"E138"),sQuery(id+"F0.wireOp",EDGE,"E139"),sQuery(id+"F0.wireOp",EDGE,"E140"),sQuery(id+"F0.wireOp",EDGE,"E141"),sQuery(id+"F0.wireOp",EDGE,"E142"),sQuery(id+"F0.wireOp",EDGE,"E143"),sQuery(id+"F0.wireOp",EDGE,"E144"),sQuery(id+"F0.wireOp",EDGE,"E145"),sQuery(id+"F0.wireOp",EDGE,"E146"),sQuery(id+"F0.wireOp",EDGE,"E147"),sQuery(id+"F0.wireOp",EDGE,"E148"),sQuery(id+"F0.wireOp",EDGE,"E149"),sQuery(id+"F0.wireOp",EDGE,"E150"),sQuery(id+"F0.wireOp",EDGE,"E151"),sQuery(id+"F0.wireOp",EDGE,"E152"),sQuery(id+"F0.wireOp",EDGE,"E153"),sQuery(id+"F0.wireOp",EDGE,"E154"),sQuery(id+"F0.wireOp",EDGE,"E155"),sQuery(id+"F0.wireOp",EDGE,"E156"),sQuery(id+"F0.wireOp",EDGE,"E157"),sQuery(id+"F0.wireOp",EDGE,"E158"),sQuery(id+"F0.wireOp",EDGE,"E159"),sQuery(id+"F0.wireOp",EDGE,"E160"),sQuery(id+"F0.wireOp",EDGE,"E161"),sQuery(id+"F0.wireOp",EDGE,"E162"),sQuery(id+"F0.wireOp",EDGE,"E163"),sQuery(id+"F0.wireOp",EDGE,"E164"),sQuery(id+"F0.wireOp",EDGE,"E165"),sQuery(id+"F0.wireOp",EDGE,"E166"),sQuery(id+"F0.wireOp",EDGE,"E167"),sQuery(id+"F0.wireOp",EDGE,"E168"),sQuery(id+"F0.wireOp",EDGE,"E169"),sQuery(id+"F0.wireOp",EDGE,"E170"),sQuery(id+"F0.wireOp",EDGE,"E171"),sQuery(id+"F0.wireOp",EDGE,"E172"),sQuery(id+"F0.wireOp",EDGE,"E173"),sQuery(id+"F0.wireOp",EDGE,"E174"),sQuery(id+"F0.wireOp",EDGE,"E175"),sQuery(id+"F0.wireOp",EDGE,"E176"),sQuery(id+"F0.wireOp",EDGE,"E177"),sQuery(id+"F0.wireOp",EDGE,"E178"),sQuery(id+"F0.wireOp",EDGE,"E179"),sQuery(id+"F0.wireOp",EDGE,"E180"),sQuery(id+"F0.wireOp",EDGE,"E181"),sQuery(id+"F0.wireOp",EDGE,"E182"),sQuery(id+"F0.wireOp",EDGE,"E183"),sQuery(id+"F0.wireOp",EDGE,"E184"),sQuery(id+"F0.wireOp",EDGE,"E185"),sQuery(id+"F0.wireOp",EDGE,"E186"),sQuery(id+"F0.wireOp",EDGE,"E187"),sQuery(id+"F0.wireOp",EDGE,"E188"),sQuery(id+"F0.wireOp",EDGE,"E189"),sQuery(id+"F0.wireOp",EDGE,"E190"),sQuery(id+"F0.wireOp",EDGE,"E191"),sQuery(id+"F0.wireOp",EDGE,"E192"),sQuery(id+"F0.wireOp",EDGE,"E193"),sQuery(id+"F0.wireOp",EDGE,"E194"),sQuery(id+"F0.wireOp",EDGE,"E195"),sQuery(id+"F0.wireOp",EDGE,"E196"),sQuery(id+"F0.wireOp",EDGE,"E197"),sQuery(id+"F0.wireOp",EDGE,"E198"),sQuery(id+"F0.wireOp",EDGE,"E199"),sQuery(id+"F0.wireOp",EDGE,"E200"),sQuery(id+"F0.wireOp",EDGE,"E201"),sQuery(id+"F0.wireOp",EDGE,"E202"),sQuery(id+"F0.wireOp",EDGE,"E203"),sQuery(id+"F0.wireOp",EDGE,"E204"),sQuery(id+"F0.wireOp",EDGE,"E205"),sQuery(id+"F0.wireOp",EDGE,"E206"),sQuery(id+"F0.wireOp",EDGE,"E207"),sQuery(id+"F0.wireOp",EDGE,"E208"),sQuery(id+"F0.wireOp",EDGE,"E209"),sQuery(id+"F0.wireOp",EDGE,"E210"),sQuery(id+"F0.wireOp",EDGE,"E211"),sQuery(id+"F0.wireOp",EDGE,"E212"),sQuery(id+"F0.wireOp",EDGE,"E213"),sQuery(id+"F0.wireOp",EDGE,"E214"),sQuery(id+"F0.wireOp",EDGE,"E215"),sQuery(id+"F0.wireOp",EDGE,"E216"),sQuery(id+"F0.wireOp",EDGE,"E217"),sQuery(id+"F0.wireOp",EDGE,"E218"),sQuery(id+"F0.wireOp",EDGE,"E219"),sQuery(id+"F0.wireOp",EDGE,"E220"),sQuery(id+"F0.wireOp",EDGE,"E221"),sQuery(id+"F0.wireOp",EDGE,"E222"),sQuery(id+"F0.wireOp",EDGE,"E223"),sQuery(id+"F0.wireOp",EDGE,"E224"),sQuery(id+"F0.wireOp",EDGE,"E225"),sQuery(id+"F0.wireOp",EDGE,"E226"),sQuery(id+"F0.wireOp",EDGE,"E227"),sQuery(id+"F0.wireOp",EDGE,"E228"),sQuery(id+"F0.wireOp",EDGE,"E229"),sQuery(id+"F0.wireOp",EDGE,"E230"),sQuery(id+"F0.wireOp",EDGE,"E231"),sQuery(id+"F0.wireOp",EDGE,"E232"),sQuery(id+"F0.wireOp",EDGE,"E233"),sQuery(id+"F0.wireOp",EDGE,"E234"),sQuery(id+"F0.wireOp",EDGE,"E235"),sQuery(id+"F0.wireOp",EDGE,"E236"),sQuery(id+"F0.wireOp",EDGE,"E237"),sQuery(id+"F0.wireOp",EDGE,"E238"),sQuery(id+"F0.wireOp",EDGE,"E239"),sQuery(id+"F0.wireOp",EDGE,"E240"),sQuery(id+"F0.wireOp",EDGE,"E241"),sQuery(id+"F0.wireOp",EDGE,"E242"),sQuery(id+"F0.wireOp",EDGE,"E243"),sQuery(id+"F0.wireOp",EDGE,"E244"),sQuery(id+"F0.wireOp",EDGE,"E245"),sQuery(id+"F0.wireOp",EDGE,"E246"),sQuery(id+"F0.wireOp",EDGE,"E247"),sQuery(id+"F0.wireOp",EDGE,"E248"),sQuery(id+"F0.wireOp",EDGE,"E249"),sQuery(id+"F0.wireOp",EDGE,"E250"),sQuery(id+"F0.wireOp",EDGE,"E251"),sQuery(id+"F0.wireOp",EDGE,"E252"),sQuery(id+"F0.wireOp",EDGE,"E253"),sQuery(id+"F0.wireOp",EDGE,"E254"),sQuery(id+"F0.wireOp",EDGE,"E255"),sQuery(id+"F0.wireOp",EDGE,"E256"),sQuery(id+"F0.wireOp",EDGE,"E257"),sQuery(id+"F0.wireOp",EDGE,"E258"),sQuery(id+"F0.wireOp",EDGE,"E259"),sQuery(id+"F0.wireOp",EDGE,"E260"),sQuery(id+"F0.wireOp",EDGE,"E261"),sQuery(id+"F0.wireOp",EDGE,"E262"),sQuery(id+"F0.wireOp",EDGE,"E263"),sQuery(id+"F0.wireOp",EDGE,"E264"),sQuery(id+"F0.wireOp",EDGE,"E265"),sQuery(id+"F0.wireOp",EDGE,"E266"),sQuery(id+"F0.wireOp",EDGE,"E267"),sQuery(id+"F0.wireOp",EDGE,"E268"),sQuery(id+"F0.wireOp",EDGE,"E269"),sQuery(id+"F0.wireOp",EDGE,"E270"),sQuery(id+"F0.wireOp",EDGE,"E271"),sQuery(id+"F0.wireOp",EDGE,"E272"),sQuery(id+"F0.wireOp",EDGE,"E273"),sQuery(id+"F0.wireOp",EDGE,"E274"),sQuery(id+"F0.wireOp",EDGE,"E275"),sQuery(id+"F0.wireOp",EDGE,"E276"),sQuery(id+"F0.wireOp",EDGE,"E277"),sQuery(id+"F0.wireOp",EDGE,"E278"),sQuery(id+"F0.wireOp",EDGE,"E279"),sQuery(id+"F0.wireOp",EDGE,"E280"),sQuery(id+"F0.wireOp",EDGE,"E281"),sQuery(id+"F0.wireOp",EDGE,"E282"),sQuery(id+"F0.wireOp",EDGE,"E283"),sQuery(id+"F0.wireOp",EDGE,"E284"),sQuery(id+"F0.wireOp",EDGE,"E285"),sQuery(id+"F0.wireOp",EDGE,"E286"),sQuery(id+"F0.wireOp",EDGE,"E287"),sQuery(id+"F0.wireOp",EDGE,"E288"),sQuery(id+"F0.wireOp",EDGE,"E289"),sQuery(id+"F0.wireOp",EDGE,"E290"),sQuery(id+"F0.wireOp",EDGE,"E291"),sQuery(id+"F0.wireOp",EDGE,"E292"),sQuery(id+"F0.wireOp",EDGE,"E293"),sQuery(id+"F0.wireOp",EDGE,"E294"),sQuery(id+"F0.wireOp",EDGE,"E295"),sQuery(id+"F0.wireOp",EDGE,"E296"),sQuery(id+"F0.wireOp",EDGE,"E297"),sQuery(id+"F0.wireOp",EDGE,"E298"),sQuery(id+"F0.wireOp",EDGE,"E299"),sQuery(id+"F0.wireOp",EDGE,"E300"),sQuery(id+"F0.wireOp",EDGE,"E301"),sQuery(id+"F0.wireOp",EDGE,"E302"),sQuery(id+"F0.wireOp",EDGE,"E303"),sQuery(id+"F0.wireOp",EDGE,"E304"),sQuery(id+"F0.wireOp",EDGE,"E305"),sQuery(id+"F0.wireOp",EDGE,"E306"),sQuery(id+"F0.wireOp",EDGE,"E307"),sQuery(id+"F0.wireOp",EDGE,"E308"),sQuery(id+"F0.wireOp",EDGE,"E309"),sQuery(id+"F0.wireOp",EDGE,"E310"),sQuery(id+"F0.wireOp",EDGE,"E311")])]});
            booleanBodies(context, id + "F4", {"operationType" : BooleanOperationType.UNION, "tools" : qUnion([Q0, Q1, Q2, Q3, Q4, Q5, Q6, Q7, Q8, Q9, Q10])});
        }
        {
            var Q0;
            Q0=makeQuery(id+"F3.opExtrude","CAP_FACE",FACE,{"disambiguationData":[OSD([sQuery(id+"F2.wireOp",EDGE,"E412")])],"isStart":true});
            var sketch = newSketch(context, id + "F5", { "sketchPlane" : qUnion([Q0])});
            skCircle(sketch, "E413", {"center": v(-44.72, 95.32) * mm, "radius": 13.01 * mm});
            skSolve(sketch);
        }
        {
            var Q0;
            Q0=makeQuery(id+"F5.imprint","IMPRINT",FACE,{"disambiguationData":[TD([[makeQuery(id+"F5.imprint","IMPRINT",EDGE,{"derivedFrom":sQuery(id+"F5.wireOp",EDGE,"E413")}),1.0]])]});
            extrude(context, id + "F6", {"entities" : qUnion([Q0]), "depth" : 25.4 * mm, "hasSecondDirection" : true, "secondDirectionOppositeDirection" : true, "secondDirectionDepth" : 25.4 * mm});
        }
        {
            var Q0;
            Q0=makeQuery(id+"F6.opExtrude","SWEPT_BODY",BODY,{"disambiguationData":[OSD([sQuery(id+"F5.wireOp",EDGE,"E413")])]});
            var Q1;
            Q1=makeQuery(id+"F1.opExtrude","SWEPT_BODY",BODY,{"disambiguationData":[OSD([sQuery(id+"F0.wireOp",EDGE,"E0"),sQuery(id+"F0.wireOp",EDGE,"E1"),sQuery(id+"F0.wireOp",EDGE,"E2"),sQuery(id+"F0.wireOp",EDGE,"E3"),sQuery(id+"F0.wireOp",EDGE,"E4"),sQuery(id+"F0.wireOp",EDGE,"E5"),sQuery(id+"F0.wireOp",EDGE,"E6"),sQuery(id+"F0.wireOp",EDGE,"E7"),sQuery(id+"F0.wireOp",EDGE,"E8"),sQuery(id+"F0.wireOp",EDGE,"E9"),sQuery(id+"F0.wireOp",EDGE,"E10"),sQuery(id+"F0.wireOp",EDGE,"E11"),sQuery(id+"F0.wireOp",EDGE,"E12"),sQuery(id+"F0.wireOp",EDGE,"E13"),sQuery(id+"F0.wireOp",EDGE,"E14"),sQuery(id+"F0.wireOp",EDGE,"E15"),sQuery(id+"F0.wireOp",EDGE,"E16"),sQuery(id+"F0.wireOp",EDGE,"E17"),sQuery(id+"F0.wireOp",EDGE,"E18"),sQuery(id+"F0.wireOp",EDGE,"E19"),sQuery(id+"F0.wireOp",EDGE,"E20"),sQuery(id+"F0.wireOp",EDGE,"E21"),sQuery(id+"F0.wireOp",EDGE,"E22"),sQuery(id+"F0.wireOp",EDGE,"E23"),sQuery(id+"F0.wireOp",EDGE,"E24"),sQuery(id+"F0.wireOp",EDGE,"E25"),sQuery(id+"F0.wireOp",EDGE,"E26"),sQuery(id+"F0.wireOp",EDGE,"E27"),sQuery(id+"F0.wireOp",EDGE,"E28"),sQuery(id+"F0.wireOp",EDGE,"E29"),sQuery(id+"F0.wireOp",EDGE,"E30"),sQuery(id+"F0.wireOp",EDGE,"E31"),sQuery(id+"F0.wireOp",EDGE,"E32"),sQuery(id+"F0.wireOp",EDGE,"E33"),sQuery(id+"F0.wireOp",EDGE,"E34"),sQuery(id+"F0.wireOp",EDGE,"E35"),sQuery(id+"F0.wireOp",EDGE,"E36"),sQuery(id+"F0.wireOp",EDGE,"E37"),sQuery(id+"F0.wireOp",EDGE,"E38"),sQuery(id+"F0.wireOp",EDGE,"E39"),sQuery(id+"F0.wireOp",EDGE,"E40"),sQuery(id+"F0.wireOp",EDGE,"E41"),sQuery(id+"F0.wireOp",EDGE,"E42"),sQuery(id+"F0.wireOp",EDGE,"E43"),sQuery(id+"F0.wireOp",EDGE,"E44"),sQuery(id+"F0.wireOp",EDGE,"E45"),sQuery(id+"F0.wireOp",EDGE,"E46"),sQuery(id+"F0.wireOp",EDGE,"E47"),sQuery(id+"F0.wireOp",EDGE,"E48"),sQuery(id+"F0.wireOp",EDGE,"E49"),sQuery(id+"F0.wireOp",EDGE,"E50"),sQuery(id+"F0.wireOp",EDGE,"E51"),sQuery(id+"F0.wireOp",EDGE,"E52"),sQuery(id+"F0.wireOp",EDGE,"E53"),sQuery(id+"F0.wireOp",EDGE,"E54"),sQuery(id+"F0.wireOp",EDGE,"E55"),sQuery(id+"F0.wireOp",EDGE,"E56"),sQuery(id+"F0.wireOp",EDGE,"E57"),sQuery(id+"F0.wireOp",EDGE,"E58"),sQuery(id+"F0.wireOp",EDGE,"E59"),sQuery(id+"F0.wireOp",EDGE,"E60"),sQuery(id+"F0.wireOp",EDGE,"E61"),sQuery(id+"F0.wireOp",EDGE,"E62"),sQuery(id+"F0.wireOp",EDGE,"E63"),sQuery(id+"F0.wireOp",EDGE,"E64"),sQuery(id+"F0.wireOp",EDGE,"E65"),sQuery(id+"F0.wireOp",EDGE,"E66"),sQuery(id+"F0.wireOp",EDGE,"E67"),sQuery(id+"F0.wireOp",EDGE,"E68"),sQuery(id+"F0.wireOp",EDGE,"E69"),sQuery(id+"F0.wireOp",EDGE,"E70"),sQuery(id+"F0.wireOp",EDGE,"E71"),sQuery(id+"F0.wireOp",EDGE,"E72"),sQuery(id+"F0.wireOp",EDGE,"E73"),sQuery(id+"F0.wireOp",EDGE,"E74"),sQuery(id+"F0.wireOp",EDGE,"E75"),sQuery(id+"F0.wireOp",EDGE,"E76"),sQuery(id+"F0.wireOp",EDGE,"E77"),sQuery(id+"F0.wireOp",EDGE,"E78"),sQuery(id+"F0.wireOp",EDGE,"E79"),sQuery(id+"F0.wireOp",EDGE,"E80"),sQuery(id+"F0.wireOp",EDGE,"E81"),sQuery(id+"F0.wireOp",EDGE,"E82"),sQuery(id+"F0.wireOp",EDGE,"E83"),sQuery(id+"F0.wireOp",EDGE,"E84"),sQuery(id+"F0.wireOp",EDGE,"E85"),sQuery(id+"F0.wireOp",EDGE,"E86"),sQuery(id+"F0.wireOp",EDGE,"E87"),sQuery(id+"F0.wireOp",EDGE,"E88"),sQuery(id+"F0.wireOp",EDGE,"E89"),sQuery(id+"F0.wireOp",EDGE,"E90"),sQuery(id+"F0.wireOp",EDGE,"E91"),sQuery(id+"F0.wireOp",EDGE,"E92"),sQuery(id+"F0.wireOp",EDGE,"E93"),sQuery(id+"F0.wireOp",EDGE,"E94"),sQuery(id+"F0.wireOp",EDGE,"E95"),sQuery(id+"F0.wireOp",EDGE,"E96"),sQuery(id+"F0.wireOp",EDGE,"E97"),sQuery(id+"F0.wireOp",EDGE,"E98"),sQuery(id+"F0.wireOp",EDGE,"E99"),sQuery(id+"F0.wireOp",EDGE,"E100"),sQuery(id+"F0.wireOp",EDGE,"E101"),sQuery(id+"F0.wireOp",EDGE,"E102"),sQuery(id+"F0.wireOp",EDGE,"E103"),sQuery(id+"F0.wireOp",EDGE,"E104"),sQuery(id+"F0.wireOp",EDGE,"E105"),sQuery(id+"F0.wireOp",EDGE,"E106"),sQuery(id+"F0.wireOp",EDGE,"E107"),sQuery(id+"F0.wireOp",EDGE,"E108"),sQuery(id+"F0.wireOp",EDGE,"E109"),sQuery(id+"F0.wireOp",EDGE,"E110"),sQuery(id+"F0.wireOp",EDGE,"E111"),sQuery(id+"F0.wireOp",EDGE,"E112"),sQuery(id+"F0.wireOp",EDGE,"E113"),sQuery(id+"F0.wireOp",EDGE,"E114")])]});
            booleanBodies(context, id + "F7", {"operationType" : BooleanOperationType.SUBTRACTION, "tools" : qUnion([Q0]), "targets" : qUnion([Q1])});
        }
        {
            var Q0;
            Q0=makeQuery(id+"F7.opBoolean","INTERSECT",EDGE,{"derivedFrom":[makeQuery(id+"F3.opExtrude","CAP_FACE",FACE,{"disambiguationData":[OSD([sQuery(id+"F2.wireOp",EDGE,"E412")])],"isStart":true}),makeQuery(id+"F6.opExtrude","SWEPT_FACE",FACE,{"disambiguationData":[OSD([sQuery(id+"F5.wireOp",EDGE,"E413")])]})]});
            var Q1;
            Q1=makeQuery(id+"F7.opBoolean","INTERSECT",EDGE,{"derivedFrom":[makeQuery(id+"F3.opExtrude","CAP_FACE",FACE,{"disambiguationData":[OSD([sQuery(id+"F2.wireOp",EDGE,"E412")])],"isStart":false}),makeQuery(id+"F6.opExtrude","SWEPT_FACE",FACE,{"disambiguationData":[OSD([sQuery(id+"F5.wireOp",EDGE,"E413")])]})]});
            chamfer(context, id + "F8", {"entities" : qUnion([Q0, Q1]), "width" : 5.08 * mm, "tangentPropagation" : true});
        }
        {
            var Q0;
            Q0=makeQuery(id+"F3.opExtrude","CAP_EDGE",EDGE,{"disambiguationData":[OSD([sQuery(id+"F2.wireOp",EDGE,"E412")])],"isStart":true});
            chamfer(context, id + "F9", {"entities" : qUnion([Q0]), "width" : 5.08 * mm, "tangentPropagation" : true});
        }
    });
